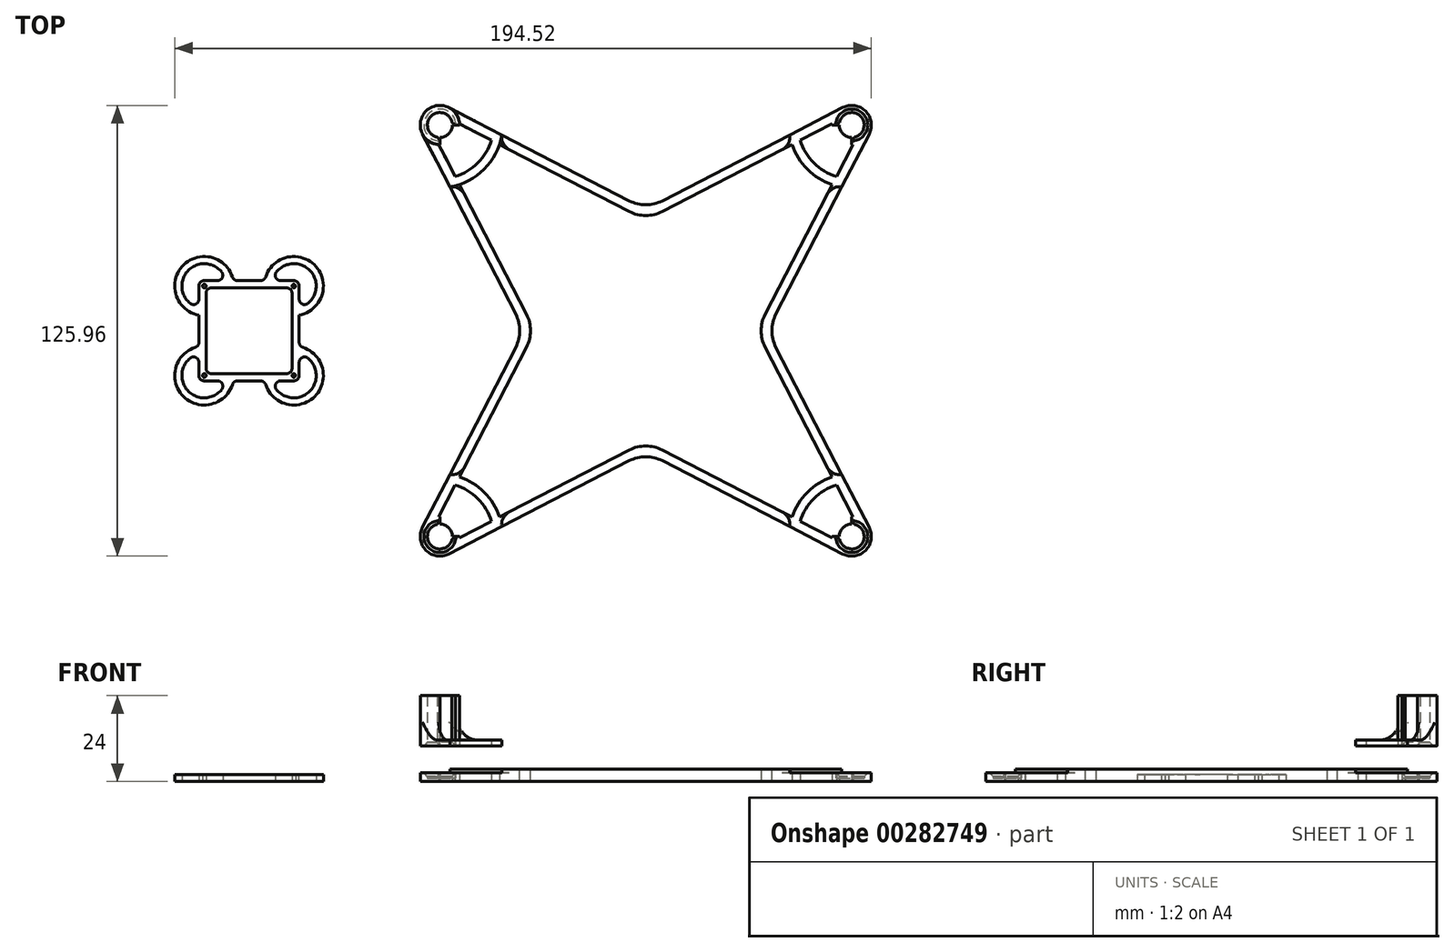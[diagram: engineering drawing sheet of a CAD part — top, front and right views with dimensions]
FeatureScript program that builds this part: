
annotation { "Feature Type Name" : "Feature", "Feature Type Description" : "" }
export const myFeature = defineFeature(function(context is Context, id is Id, definition is map)
    precondition{}
    {
        {
            var Q0;
            Q0=qCreatedBy(makeId("Top.planeOp"),FACE);
            var sketch = newSketch(context, id + "F0", { "sketchPlane" : qUnion([Q0])});
            skLineSegment(sketch, "E0.rect.bottom", {"start": v(57.5, 57.5) * mm, "end": v(-57.5, 57.5) * mm});
            skLineSegment(sketch, "E0.rect.top", {"start": v(57.5, -57.5) * mm, "end": v(-57.5, -57.5) * mm});
            skLineSegment(sketch, "E0.rect.left", {"start": v(57.5, 57.5) * mm, "end": v(57.5, -57.5) * mm});
            skLineSegment(sketch, "E0.rect.right", {"start": v(-57.5, 57.5) * mm, "end": v(-57.5, -57.5) * mm});
            skPoint(sketch, "E0.rect.middle", {"position": v(0, 0) * mm});
            skLineSegment(sketch, "E1", {"start": v(0, 33.94) * mm, "end": v(-33.94, 0) * mm});
            skLineSegment(sketch, "E2", {"start": v(-33.94, 0) * mm, "end": v(0, -33.94) * mm});
            skLineSegment(sketch, "E3", {"start": v(0, -33.94) * mm, "end": v(33.94, 0) * mm});
            skLineSegment(sketch, "E4", {"start": v(33.94, 0) * mm, "end": v(0, 33.94) * mm});
            skCircle(sketch, "E5", {"center": v(57.5, 57.5) * mm, "radius": 3.48 * mm});
            skCircle(sketch, "E6", {"center": v(57.5, 57.5) * mm, "radius": 5.47 * mm});
            skLineSegment(sketch, "E7", {"start": v(57.5, 60.98) * mm, "end": v(57.5, 62.98) * mm, "construction": true});
            skCircle(sketch, "E8", {"center": v(-57.5, 57.5) * mm, "radius": 3.48 * mm});
            skCircle(sketch, "E9", {"center": v(-57.5, 57.5) * mm, "radius": 5.47 * mm});
            skCircle(sketch, "E10", {"center": v(-57.5, -57.5) * mm, "radius": 3.48 * mm});
            skCircle(sketch, "E11", {"center": v(-57.5, -57.5) * mm, "radius": 5.47 * mm});
            skCircle(sketch, "E12", {"center": v(57.5, -57.5) * mm, "radius": 3.48 * mm});
            skCircle(sketch, "E13", {"center": v(57.5, -57.5) * mm, "radius": 5.47 * mm});
            skLineSegment(sketch, "E14", {"start": v(62.36, 54.99) * mm, "end": v(33.94, 0) * mm});
            skLineSegment(sketch, "E15", {"start": v(33.94, 0) * mm, "end": v(62.36, -54.99) * mm});
            skLineSegment(sketch, "E16", {"start": v(54.99, -62.36) * mm, "end": v(0, -33.94) * mm});
            skLineSegment(sketch, "E17", {"start": v(0, -33.94) * mm, "end": v(-54.99, -62.36) * mm});
            skLineSegment(sketch, "E18", {"start": v(-62.36, -54.99) * mm, "end": v(-33.94, 0) * mm});
            skLineSegment(sketch, "E19", {"start": v(-33.94, 0) * mm, "end": v(-62.36, 54.99) * mm});
            skLineSegment(sketch, "E20", {"start": v(-54.99, 62.36) * mm, "end": v(0, 33.94) * mm});
            skLineSegment(sketch, "E21", {"start": v(0, 33.94) * mm, "end": v(54.99, 62.36) * mm});
            skLineSegment(sketch, "E22.0", {"start": v(30.94, 0) * mm, "end": v(0, 30.94) * mm});
            skLineSegment(sketch, "E22.1", {"start": v(0, -30.94) * mm, "end": v(30.94, 0) * mm});
            skLineSegment(sketch, "E22.2", {"start": v(-30.94, 0) * mm, "end": v(0, -30.94) * mm});
            skLineSegment(sketch, "E22.3", {"start": v(0, 30.94) * mm, "end": v(-30.94, 0) * mm});
            skLineSegment(sketch, "E23", {"start": v(-30.94, 0) * mm, "end": v(-57.84, 52.04) * mm});
            skLineSegment(sketch, "E24", {"start": v(-30.94, 0) * mm, "end": v(-57.84, -52.04) * mm});
            skLineSegment(sketch, "E25", {"start": v(30.94, 0) * mm, "end": v(33.94, 0) * mm, "construction": true});
            skLineSegment(sketch, "E26", {"start": v(0, -30.94) * mm, "end": v(-52.04, -57.84) * mm});
            skLineSegment(sketch, "E27", {"start": v(0, -30.94) * mm, "end": v(52.04, -57.84) * mm});
            skLineSegment(sketch, "E28", {"start": v(57.84, -52.04) * mm, "end": v(30.94, 0) * mm});
            skLineSegment(sketch, "E29", {"start": v(30.94, 0) * mm, "end": v(57.84, 52.04) * mm});
            skLineSegment(sketch, "E30", {"start": v(52.04, 57.84) * mm, "end": v(0, 30.94) * mm});
            skLineSegment(sketch, "E31", {"start": v(0, 30.94) * mm, "end": v(-52.04, 57.84) * mm});
            skCircle(sketch, "E32", {"center": v(57.5, 57.5) * mm, "radius": 15 * mm});
            skCircle(sketch, "E33", {"center": v(57.5, 57.5) * mm, "radius": 17.5 * mm});
            skLineSegment(sketch, "E34", {"start": v(57.5, 72.5) * mm, "end": v(57.5, 75) * mm, "construction": true});
            skCircle(sketch, "E35", {"center": v(-57.5, 57.5) * mm, "radius": 15 * mm});
            skCircle(sketch, "E36", {"center": v(-57.5, 57.5) * mm, "radius": 17.5 * mm});
            skCircle(sketch, "E37", {"center": v(-57.5, -57.5) * mm, "radius": 15 * mm});
            skCircle(sketch, "E38", {"center": v(-57.5, -57.5) * mm, "radius": 17.5 * mm});
            skCircle(sketch, "E39", {"center": v(57.5, -57.5) * mm, "radius": 15 * mm});
            skCircle(sketch, "E40", {"center": v(57.5, -57.5) * mm, "radius": 17.5 * mm});
            skLineSegment(sketch, "E41.rect.bottom", {"start": v(-98.29, 12.5) * mm, "end": v(-123.29, 12.5) * mm, "construction": true});
            skLineSegment(sketch, "E41.rect.top", {"start": v(-98.29, -12.5) * mm, "end": v(-123.29, -12.5) * mm, "construction": true});
            skLineSegment(sketch, "E41.rect.left", {"start": v(-98.29, 12.5) * mm, "end": v(-98.29, -12.5) * mm, "construction": true});
            skLineSegment(sketch, "E41.rect.right", {"start": v(-123.29, 12.5) * mm, "end": v(-123.29, -12.5) * mm, "construction": true});
            skPoint(sketch, "E41.rect.middle", {"position": v(-110.79, 0) * mm});
            skCircle(sketch, "E42", {"center": v(-98.29, 12.5) * mm, "radius": 0.5 * mm});
            skCircle(sketch, "E43", {"center": v(-98.29, -12.5) * mm, "radius": 0.5 * mm});
            skCircle(sketch, "E44", {"center": v(-123.29, -12.5) * mm, "radius": 0.5 * mm});
            skCircle(sketch, "E45", {"center": v(-123.29, 12.5) * mm, "radius": 0.5 * mm});
            skCircle(sketch, "E46", {"center": v(-98.29, 12.5) * mm, "radius": 6.25 * mm});
            skCircle(sketch, "E47", {"center": v(-123.29, 12.5) * mm, "radius": 6.25 * mm});
            skCircle(sketch, "E48", {"center": v(-123.29, -12.5) * mm, "radius": 6.25 * mm});
            skCircle(sketch, "E49", {"center": v(-98.29, -12.5) * mm, "radius": 6.25 * mm});
            skCircle(sketch, "E50", {"center": v(-98.29, 12.5) * mm, "radius": 8.25 * mm});
            skLineSegment(sketch, "E51", {"start": v(-98.29, 18.75) * mm, "end": v(-98.29, 20.75) * mm, "construction": true});
            skCircle(sketch, "E52", {"center": v(-123.29, 12.5) * mm, "radius": 8.25 * mm});
            skCircle(sketch, "E53", {"center": v(-123.29, -12.5) * mm, "radius": 8.25 * mm});
            skCircle(sketch, "E54", {"center": v(-98.29, -12.5) * mm, "radius": 8.25 * mm});
            skLineSegment(sketch, "E55.rect.bottom", {"start": v(-96.79, 14) * mm, "end": v(-124.79, 14) * mm});
            skLineSegment(sketch, "E55.rect.top", {"start": v(-96.79, -14) * mm, "end": v(-124.79, -14) * mm});
            skLineSegment(sketch, "E55.rect.left", {"start": v(-96.79, 14) * mm, "end": v(-96.79, -14) * mm});
            skLineSegment(sketch, "E55.rect.right", {"start": v(-124.79, 14) * mm, "end": v(-124.79, -14) * mm});
            skLineSegment(sketch, "E56.rect.bottom", {"start": v(-98.79, 12) * mm, "end": v(-122.79, 12) * mm});
            skLineSegment(sketch, "E56.rect.top", {"start": v(-98.79, -12) * mm, "end": v(-122.79, -12) * mm});
            skLineSegment(sketch, "E56.rect.left", {"start": v(-98.79, 12) * mm, "end": v(-98.79, -12) * mm});
            skLineSegment(sketch, "E56.rect.right", {"start": v(-122.79, 12) * mm, "end": v(-122.79, -12) * mm});
            skLineSegment(sketch, "E57", {"start": v(-110.79, 12.5) * mm, "end": v(-110.79, 14) * mm, "construction": true});
            skLineSegment(sketch, "E58", {"start": v(-110.79, 12.5) * mm, "end": v(-110.79, 12) * mm, "construction": true});
            skCircle(sketch, "E59.cCircle", {"center": v(-110.79, 0) * mm, "radius": 17.68 * mm, "construction": true});
            skLineSegment(sketch, "E59.0", {"start": v(-110.79, 25) * mm, "end": v(-85.79, 0) * mm});
            skLineSegment(sketch, "E59.1", {"start": v(-85.79, 0) * mm, "end": v(-110.79, -25) * mm});
            skLineSegment(sketch, "E59.2", {"start": v(-110.79, -25) * mm, "end": v(-135.79, 0) * mm});
            skLineSegment(sketch, "E59.3", {"start": v(-135.79, 0) * mm, "end": v(-110.79, 25) * mm});
            skLineSegment(sketch, "E60", {"start": v(-124.79, 14) * mm, "end": v(-124.79, 20.61) * mm});
            skLineSegment(sketch, "E61", {"start": v(-122.79, 14) * mm, "end": v(-122.79, 20.73) * mm});
            skLineSegment(sketch, "E62", {"start": v(-98.79, 14) * mm, "end": v(-98.79, 20.73) * mm});
            skLineSegment(sketch, "E63", {"start": v(-96.79, 14) * mm, "end": v(-96.79, 20.61) * mm});
            skLineSegment(sketch, "E64", {"start": v(-124.79, -14) * mm, "end": v(-124.79, -20.61) * mm});
            skLineSegment(sketch, "E65", {"start": v(-122.79, -14) * mm, "end": v(-122.79, -20.73) * mm});
            skLineSegment(sketch, "E66", {"start": v(-98.79, -14) * mm, "end": v(-98.79, -20.73) * mm});
            skLineSegment(sketch, "E67", {"start": v(-96.79, -14) * mm, "end": v(-96.79, -20.61) * mm});
            skSolve(sketch);
        }
        {
            var Q0;
            {var subQ0=sQuery(id+"F0.wireOp",EDGE,"E9");var subQ7=sQuery(id+"F0.wireOp",EDGE,"E0.rect.bottom");var subQ8=makeQuery(id+"F0.imprint","INTERSECT",VERTEX,{"derivedFrom":[subQ7,subQ0]});Q0=makeQuery(id+"F0.imprint","IMPRINT",FACE,{"disambiguationData":[TD([[makeQuery(id+"F0.imprint","IMPRINT",EDGE,{"disambiguationData":[TD([[subQ8,-1.0]])],"derivedFrom":subQ7}),-1.0]])]});}
            var Q1;
            {var subQ1=sQuery(id+"F0.wireOp",EDGE,"E0.rect.right");var subQ5=sQuery(id+"F0.wireOp",EDGE,"E23");var subQ6=makeQuery(id+"F0.imprint","INTERSECT",VERTEX,{"derivedFrom":[subQ1,subQ5]});Q1=makeQuery(id+"F0.imprint","IMPRINT",FACE,{"disambiguationData":[TD([[makeQuery(id+"F0.imprint","IMPRINT",EDGE,{"disambiguationData":[TD([[subQ6,-1.0]])],"derivedFrom":subQ1}),-1.0]])]});}
            var Q2;
            {var subQ1=sQuery(id+"F0.wireOp",EDGE,"E23");var subQ5=sQuery(id+"F0.wireOp",EDGE,"E0.rect.right");var subQ6=makeQuery(id+"F0.imprint","INTERSECT",VERTEX,{"derivedFrom":[subQ5,subQ1]});Q2=makeQuery(id+"F0.imprint","IMPRINT",FACE,{"disambiguationData":[TD([[makeQuery(id+"F0.imprint","IMPRINT",EDGE,{"disambiguationData":[TD([[subQ6,-1.0]])],"derivedFrom":subQ5}),1.0]])]});}
            var Q3;
            {var subQ1=sQuery(id+"F0.wireOp",EDGE,"E0.rect.bottom");var subQ5=sQuery(id+"F0.wireOp",EDGE,"E20");var subQ6=makeQuery(id+"F0.imprint","INTERSECT",VERTEX,{"derivedFrom":[subQ1,subQ5]});Q3=makeQuery(id+"F0.imprint","IMPRINT",FACE,{"disambiguationData":[TD([[makeQuery(id+"F0.imprint","IMPRINT",EDGE,{"disambiguationData":[TD([[subQ6,-1.0]])],"derivedFrom":subQ1}),-1.0]])]});}
            var Q4;
            {var subQ3=sQuery(id+"F0.wireOp",EDGE,"E20");var subQ5=sQuery(id+"F0.wireOp",EDGE,"E0.rect.bottom");var subQ7=makeQuery(id+"F0.imprint","INTERSECT",VERTEX,{"derivedFrom":[subQ5,subQ3]});Q4=makeQuery(id+"F0.imprint","IMPRINT",FACE,{"disambiguationData":[TD([[makeQuery(id+"F0.imprint","IMPRINT",EDGE,{"disambiguationData":[TD([[subQ7,-1.0]])],"derivedFrom":subQ5}),1.0]])]});}
            var Q5;
            {var subQ0=sQuery(id+"F0.wireOp",EDGE,"E36");var subQ3=sQuery(id+"F0.wireOp",EDGE,"E19");var subQ4=makeQuery(id+"F0.imprint","INTERSECT",VERTEX,{"derivedFrom":[subQ3,subQ0]});Q5=makeQuery(id+"F0.imprint","IMPRINT",FACE,{"disambiguationData":[TD([[makeQuery(id+"F0.imprint","IMPRINT",EDGE,{"disambiguationData":[TD([[subQ4,-1.0]])],"derivedFrom":subQ3}),-1.0]])]});}
            var Q6;
            {var subQ3=sQuery(id+"F0.wireOp",EDGE,"E23");var subQ5=sQuery(id+"F0.wireOp",EDGE,"E36");var subQ7=makeQuery(id+"F0.imprint","INTERSECT",VERTEX,{"derivedFrom":[subQ3,subQ5]});Q6=makeQuery(id+"F0.imprint","IMPRINT",FACE,{"disambiguationData":[TD([[makeQuery(id+"F0.imprint","IMPRINT",EDGE,{"disambiguationData":[TD([[subQ7,-1.0]])],"derivedFrom":subQ3}),-1.0]])]});}
            var Q7;
            {var subQ3=sQuery(id+"F0.wireOp",EDGE,"E20");var subQ5=sQuery(id+"F0.wireOp",EDGE,"E35");var subQ7=makeQuery(id+"F0.imprint","INTERSECT",VERTEX,{"derivedFrom":[subQ3,subQ5]});Q7=makeQuery(id+"F0.imprint","IMPRINT",FACE,{"disambiguationData":[TD([[makeQuery(id+"F0.imprint","IMPRINT",EDGE,{"disambiguationData":[TD([[subQ7,-1.0]])],"derivedFrom":subQ3}),-1.0]])]});}
            extrude(context, id + "F1", {"entities" : qUnion([Q0, Q1, Q2, Q3, Q4, Q5, Q6, Q7]), "depth" : 1.6 * mm});
        }
        {
            var Q0;
            {var subQ0=sQuery(id+"F0.wireOp",EDGE,"E9");var subQ7=sQuery(id+"F0.wireOp",EDGE,"E0.rect.bottom");var subQ8=makeQuery(id+"F0.imprint","INTERSECT",VERTEX,{"derivedFrom":[subQ7,subQ0]});Q0=makeQuery(id+"F0.imprint","IMPRINT",FACE,{"disambiguationData":[TD([[makeQuery(id+"F0.imprint","IMPRINT",EDGE,{"disambiguationData":[TD([[subQ8,-1.0]])],"derivedFrom":subQ7}),-1.0]])]});}
            extrude(context, id + "F2", {"entities" : qUnion([Q0]), "operationType" : NewBodyOperationType.ADD, "depth" : 14 * mm});
        }
        {
            var Q0;
            {var subQ0=sQuery(id+"F0.wireOp",EDGE,"E9");Q0=makeQuery(id+"F2.boolean.opBoolean","INTERSECT",EDGE,{"disambiguationData":[OD(0.0)],"derivedFrom":[makeQuery(id+"F1.opExtrude","CAP_FACE",FACE,{"disambiguationData":[OSD([sQuery(id+"F0.wireOp",EDGE,"E0.rect.bottom"),sQuery(id+"F0.wireOp",EDGE,"E0.rect.right"),sQuery(id+"F0.wireOp",EDGE,"E8"),subQ0,sQuery(id+"F0.wireOp",EDGE,"E19"),sQuery(id+"F0.wireOp",EDGE,"E20"),sQuery(id+"F0.wireOp",EDGE,"E23"),sQuery(id+"F0.wireOp",EDGE,"E31"),sQuery(id+"F0.wireOp",EDGE,"E35"),sQuery(id+"F0.wireOp",EDGE,"E36")])],"isStart":false}),makeQuery(id+"F2.opExtrude","SWEPT_FACE",FACE,{"disambiguationData":[OSD([subQ0])]})]});}
            var Q1;
            {var subQ0=sQuery(id+"F0.wireOp",EDGE,"E9");Q1=makeQuery(id+"F2.boolean.opBoolean","INTERSECT",EDGE,{"disambiguationData":[OD(1.0)],"derivedFrom":[makeQuery(id+"F1.opExtrude","CAP_FACE",FACE,{"disambiguationData":[OSD([sQuery(id+"F0.wireOp",EDGE,"E0.rect.bottom"),sQuery(id+"F0.wireOp",EDGE,"E0.rect.right"),sQuery(id+"F0.wireOp",EDGE,"E8"),subQ0,sQuery(id+"F0.wireOp",EDGE,"E19"),sQuery(id+"F0.wireOp",EDGE,"E20"),sQuery(id+"F0.wireOp",EDGE,"E23"),sQuery(id+"F0.wireOp",EDGE,"E31"),sQuery(id+"F0.wireOp",EDGE,"E35"),sQuery(id+"F0.wireOp",EDGE,"E36")])],"isStart":false}),makeQuery(id+"F2.opExtrude","SWEPT_FACE",FACE,{"disambiguationData":[OSD([subQ0])]})]});}
            fillet(context, id + "F3", {"entities" : qUnion([Q0, Q1]), "radius" : 5 * mm, "tangentPropagation" : true, "allowEdgeOverflow" : false});
        }
        {
            var Q0;
            Q0=makeQuery(id+"F1.opExtrude","SWEPT_BODY",BODY,{"disambiguationData":[OSD([sQuery(id+"F0.wireOp",EDGE,"E0.rect.bottom"),sQuery(id+"F0.wireOp",EDGE,"E0.rect.right"),sQuery(id+"F0.wireOp",EDGE,"E8"),sQuery(id+"F0.wireOp",EDGE,"E9"),sQuery(id+"F0.wireOp",EDGE,"E19"),sQuery(id+"F0.wireOp",EDGE,"E20"),sQuery(id+"F0.wireOp",EDGE,"E23"),sQuery(id+"F0.wireOp",EDGE,"E31"),sQuery(id+"F0.wireOp",EDGE,"E35"),sQuery(id+"F0.wireOp",EDGE,"E36")])]});
            transform(context, id + "F4", {"entities" : qUnion([Q0]), "transformType" : TransformType.TRANSLATION_3D, "dx" : 0 * mm, "dy" : 0 * mm, "dz" : 10 * mm, "makeCopy" : false});
        }
        {
            var Q0;
            {var subQ1=sQuery(id+"F0.wireOp",EDGE,"E23");var subQ5=sQuery(id+"F0.wireOp",EDGE,"E0.rect.right");var subQ6=makeQuery(id+"F0.imprint","INTERSECT",VERTEX,{"derivedFrom":[subQ5,subQ1]});Q0=makeQuery(id+"F0.imprint","IMPRINT",FACE,{"disambiguationData":[TD([[makeQuery(id+"F0.imprint","IMPRINT",EDGE,{"disambiguationData":[TD([[subQ6,-1.0]])],"derivedFrom":subQ5}),1.0]])]});}
            var Q1;
            {var subQ1=sQuery(id+"F0.wireOp",EDGE,"E0.rect.right");var subQ5=sQuery(id+"F0.wireOp",EDGE,"E23");var subQ6=makeQuery(id+"F0.imprint","INTERSECT",VERTEX,{"derivedFrom":[subQ1,subQ5]});Q1=makeQuery(id+"F0.imprint","IMPRINT",FACE,{"disambiguationData":[TD([[makeQuery(id+"F0.imprint","IMPRINT",EDGE,{"disambiguationData":[TD([[subQ6,-1.0]])],"derivedFrom":subQ1}),-1.0]])]});}
            var Q2;
            {var subQ0=sQuery(id+"F0.wireOp",EDGE,"E9");var subQ7=sQuery(id+"F0.wireOp",EDGE,"E0.rect.bottom");var subQ8=makeQuery(id+"F0.imprint","INTERSECT",VERTEX,{"derivedFrom":[subQ7,subQ0]});Q2=makeQuery(id+"F0.imprint","IMPRINT",FACE,{"disambiguationData":[TD([[makeQuery(id+"F0.imprint","IMPRINT",EDGE,{"disambiguationData":[TD([[subQ8,-1.0]])],"derivedFrom":subQ7}),-1.0]])]});}
            var Q3;
            {var subQ1=sQuery(id+"F0.wireOp",EDGE,"E0.rect.bottom");var subQ5=sQuery(id+"F0.wireOp",EDGE,"E20");var subQ6=makeQuery(id+"F0.imprint","INTERSECT",VERTEX,{"derivedFrom":[subQ1,subQ5]});Q3=makeQuery(id+"F0.imprint","IMPRINT",FACE,{"disambiguationData":[TD([[makeQuery(id+"F0.imprint","IMPRINT",EDGE,{"disambiguationData":[TD([[subQ6,-1.0]])],"derivedFrom":subQ1}),-1.0]])]});}
            var Q4;
            {var subQ3=sQuery(id+"F0.wireOp",EDGE,"E20");var subQ5=sQuery(id+"F0.wireOp",EDGE,"E0.rect.bottom");var subQ7=makeQuery(id+"F0.imprint","INTERSECT",VERTEX,{"derivedFrom":[subQ5,subQ3]});Q4=makeQuery(id+"F0.imprint","IMPRINT",FACE,{"disambiguationData":[TD([[makeQuery(id+"F0.imprint","IMPRINT",EDGE,{"disambiguationData":[TD([[subQ7,-1.0]])],"derivedFrom":subQ5}),1.0]])]});}
            var Q5;
            {var subQ0=sQuery(id+"F0.wireOp",EDGE,"E36");var subQ3=sQuery(id+"F0.wireOp",EDGE,"E19");var subQ4=makeQuery(id+"F0.imprint","INTERSECT",VERTEX,{"derivedFrom":[subQ3,subQ0]});Q5=makeQuery(id+"F0.imprint","IMPRINT",FACE,{"disambiguationData":[TD([[makeQuery(id+"F0.imprint","IMPRINT",EDGE,{"disambiguationData":[TD([[subQ4,-1.0]])],"derivedFrom":subQ3}),-1.0]])]});}
            var Q6;
            {var subQ3=sQuery(id+"F0.wireOp",EDGE,"E20");var subQ5=sQuery(id+"F0.wireOp",EDGE,"E35");var subQ7=makeQuery(id+"F0.imprint","INTERSECT",VERTEX,{"derivedFrom":[subQ3,subQ5]});Q6=makeQuery(id+"F0.imprint","IMPRINT",FACE,{"disambiguationData":[TD([[makeQuery(id+"F0.imprint","IMPRINT",EDGE,{"disambiguationData":[TD([[subQ7,-1.0]])],"derivedFrom":subQ3}),-1.0]])]});}
            var Q7;
            {var subQ0=sQuery(id+"F0.wireOp",EDGE,"E33");var subQ3=sQuery(id+"F0.wireOp",EDGE,"E21");var subQ4=makeQuery(id+"F0.imprint","INTERSECT",VERTEX,{"derivedFrom":[subQ3,subQ0]});Q7=makeQuery(id+"F0.imprint","IMPRINT",FACE,{"disambiguationData":[TD([[makeQuery(id+"F0.imprint","IMPRINT",EDGE,{"disambiguationData":[TD([[subQ4,-1.0]])],"derivedFrom":subQ3}),-1.0]])]});}
            var Q8;
            {var subQ1=sQuery(id+"F0.wireOp",EDGE,"E30");var subQ5=sQuery(id+"F0.wireOp",EDGE,"E0.rect.bottom");var subQ6=makeQuery(id+"F0.imprint","INTERSECT",VERTEX,{"derivedFrom":[subQ5,subQ1]});Q8=makeQuery(id+"F0.imprint","IMPRINT",FACE,{"disambiguationData":[TD([[makeQuery(id+"F0.imprint","IMPRINT",EDGE,{"disambiguationData":[TD([[subQ6,-1.0]])],"derivedFrom":subQ5}),1.0]])]});}
            var Q9;
            {var subQ0=sQuery(id+"F0.wireOp",EDGE,"E30");var subQ1=sQuery(id+"F0.wireOp",EDGE,"E0.rect.bottom");var subQ2=makeQuery(id+"F0.imprint","INTERSECT",VERTEX,{"derivedFrom":[subQ1,subQ0]});Q9=makeQuery(id+"F0.imprint","IMPRINT",FACE,{"disambiguationData":[TD([[makeQuery(id+"F0.imprint","IMPRINT",EDGE,{"disambiguationData":[TD([[subQ2,-1.0]])],"derivedFrom":subQ1}),-1.0]])]});}
            var Q10;
            {var subQ7=sQuery(id+"F0.wireOp",EDGE,"E5");var subQ9=sQuery(id+"F0.wireOp",EDGE,"E0.rect.bottom");var subQ10=makeQuery(id+"F0.imprint","INTERSECT",VERTEX,{"derivedFrom":[subQ9,subQ7]});Q10=makeQuery(id+"F0.imprint","IMPRINT",FACE,{"disambiguationData":[TD([[makeQuery(id+"F0.imprint","IMPRINT",EDGE,{"disambiguationData":[TD([[subQ10,-1.0]])],"derivedFrom":subQ9}),-1.0]])]});}
            var Q11;
            {var subQ0=sQuery(id+"F0.wireOp",EDGE,"E29");var subQ1=sQuery(id+"F0.wireOp",EDGE,"E0.rect.left");var subQ2=makeQuery(id+"F0.imprint","INTERSECT",VERTEX,{"derivedFrom":[subQ1,subQ0]});Q11=makeQuery(id+"F0.imprint","IMPRINT",FACE,{"disambiguationData":[TD([[makeQuery(id+"F0.imprint","IMPRINT",EDGE,{"disambiguationData":[TD([[subQ2,-1.0]])],"derivedFrom":subQ1}),1.0]])]});}
            var Q12;
            {var subQ1=sQuery(id+"F0.wireOp",EDGE,"E29");var subQ5=sQuery(id+"F0.wireOp",EDGE,"E0.rect.left");var subQ6=makeQuery(id+"F0.imprint","INTERSECT",VERTEX,{"derivedFrom":[subQ5,subQ1]});Q12=makeQuery(id+"F0.imprint","IMPRINT",FACE,{"disambiguationData":[TD([[makeQuery(id+"F0.imprint","IMPRINT",EDGE,{"disambiguationData":[TD([[subQ6,-1.0]])],"derivedFrom":subQ5}),-1.0]])]});}
            var Q13;
            {var subQ3=sQuery(id+"F0.wireOp",EDGE,"E14");var subQ5=sQuery(id+"F0.wireOp",EDGE,"E32");var subQ7=makeQuery(id+"F0.imprint","INTERSECT",VERTEX,{"derivedFrom":[subQ3,subQ5]});Q13=makeQuery(id+"F0.imprint","IMPRINT",FACE,{"disambiguationData":[TD([[makeQuery(id+"F0.imprint","IMPRINT",EDGE,{"disambiguationData":[TD([[subQ7,-1.0]])],"derivedFrom":subQ3}),-1.0]])]});}
            var Q14;
            {var subQ0=sQuery(id+"F0.wireOp",EDGE,"E40");var subQ3=sQuery(id+"F0.wireOp",EDGE,"E15");var subQ4=makeQuery(id+"F0.imprint","INTERSECT",VERTEX,{"derivedFrom":[subQ3,subQ0]});Q14=makeQuery(id+"F0.imprint","IMPRINT",FACE,{"disambiguationData":[TD([[makeQuery(id+"F0.imprint","IMPRINT",EDGE,{"disambiguationData":[TD([[subQ4,-1.0]])],"derivedFrom":subQ3}),-1.0]])]});}
            var Q15;
            {var subQ3=sQuery(id+"F0.wireOp",EDGE,"E18");var subQ5=sQuery(id+"F0.wireOp",EDGE,"E37");var subQ7=makeQuery(id+"F0.imprint","INTERSECT",VERTEX,{"derivedFrom":[subQ3,subQ5]});Q15=makeQuery(id+"F0.imprint","IMPRINT",FACE,{"disambiguationData":[TD([[makeQuery(id+"F0.imprint","IMPRINT",EDGE,{"disambiguationData":[TD([[subQ7,-1.0]])],"derivedFrom":subQ3}),-1.0]])]});}
            var Q16;
            {var subQ3=sQuery(id+"F0.wireOp",EDGE,"E18");var subQ5=sQuery(id+"F0.wireOp",EDGE,"E0.rect.right");var subQ7=makeQuery(id+"F0.imprint","INTERSECT",VERTEX,{"derivedFrom":[subQ5,subQ3]});Q16=makeQuery(id+"F0.imprint","IMPRINT",FACE,{"disambiguationData":[TD([[makeQuery(id+"F0.imprint","IMPRINT",EDGE,{"disambiguationData":[TD([[subQ7,-1.0]])],"derivedFrom":subQ5}),1.0]])]});}
            var Q17;
            {var subQ1=sQuery(id+"F0.wireOp",EDGE,"E0.rect.right");var subQ5=sQuery(id+"F0.wireOp",EDGE,"E18");var subQ6=makeQuery(id+"F0.imprint","INTERSECT",VERTEX,{"derivedFrom":[subQ1,subQ5]});Q17=makeQuery(id+"F0.imprint","IMPRINT",FACE,{"disambiguationData":[TD([[makeQuery(id+"F0.imprint","IMPRINT",EDGE,{"disambiguationData":[TD([[subQ6,-1.0]])],"derivedFrom":subQ1}),-1.0]])]});}
            var Q18;
            {var subQ0=sQuery(id+"F0.wireOp",EDGE,"E11");var subQ1=sQuery(id+"F0.wireOp",EDGE,"E0.rect.top");var subQ2=makeQuery(id+"F0.imprint","INTERSECT",VERTEX,{"derivedFrom":[subQ1,subQ0]});Q18=makeQuery(id+"F0.imprint","IMPRINT",FACE,{"disambiguationData":[TD([[makeQuery(id+"F0.imprint","IMPRINT",EDGE,{"disambiguationData":[TD([[subQ2,-1.0]])],"derivedFrom":subQ1}),1.0]])]});}
            var Q19;
            {var subQ1=sQuery(id+"F0.wireOp",EDGE,"E0.rect.top");var subQ5=sQuery(id+"F0.wireOp",EDGE,"E17");var subQ6=makeQuery(id+"F0.imprint","INTERSECT",VERTEX,{"derivedFrom":[subQ1,subQ5]});Q19=makeQuery(id+"F0.imprint","IMPRINT",FACE,{"disambiguationData":[TD([[makeQuery(id+"F0.imprint","IMPRINT",EDGE,{"disambiguationData":[TD([[subQ6,-1.0]])],"derivedFrom":subQ1}),1.0]])]});}
            var Q20;
            {var subQ3=sQuery(id+"F0.wireOp",EDGE,"E17");var subQ5=sQuery(id+"F0.wireOp",EDGE,"E0.rect.top");var subQ7=makeQuery(id+"F0.imprint","INTERSECT",VERTEX,{"derivedFrom":[subQ5,subQ3]});Q20=makeQuery(id+"F0.imprint","IMPRINT",FACE,{"disambiguationData":[TD([[makeQuery(id+"F0.imprint","IMPRINT",EDGE,{"disambiguationData":[TD([[subQ7,-1.0]])],"derivedFrom":subQ5}),-1.0]])]});}
            var Q21;
            {var subQ0=sQuery(id+"F0.wireOp",EDGE,"E38");var subQ3=sQuery(id+"F0.wireOp",EDGE,"E17");var subQ4=makeQuery(id+"F0.imprint","INTERSECT",VERTEX,{"derivedFrom":[subQ3,subQ0]});Q21=makeQuery(id+"F0.imprint","IMPRINT",FACE,{"disambiguationData":[TD([[makeQuery(id+"F0.imprint","IMPRINT",EDGE,{"disambiguationData":[TD([[subQ4,-1.0]])],"derivedFrom":subQ3}),-1.0]])]});}
            var Q22;
            {var subQ3=sQuery(id+"F0.wireOp",EDGE,"E16");var subQ5=sQuery(id+"F0.wireOp",EDGE,"E39");var subQ7=makeQuery(id+"F0.imprint","INTERSECT",VERTEX,{"derivedFrom":[subQ3,subQ5]});Q22=makeQuery(id+"F0.imprint","IMPRINT",FACE,{"disambiguationData":[TD([[makeQuery(id+"F0.imprint","IMPRINT",EDGE,{"disambiguationData":[TD([[subQ7,-1.0]])],"derivedFrom":subQ3}),-1.0]])]});}
            var Q23;
            {var subQ3=sQuery(id+"F0.wireOp",EDGE,"E0.rect.top");var subQ9=sQuery(id+"F0.wireOp",EDGE,"E12");var subQ11=makeQuery(id+"F0.imprint","INTERSECT",VERTEX,{"derivedFrom":[subQ3,subQ9]});Q23=makeQuery(id+"F0.imprint","IMPRINT",FACE,{"disambiguationData":[TD([[makeQuery(id+"F0.imprint","IMPRINT",EDGE,{"disambiguationData":[TD([[subQ11,-1.0]])],"derivedFrom":subQ3}),1.0]])]});}
            var Q24;
            {var subQ1=sQuery(id+"F0.wireOp",EDGE,"E0.rect.top");var subQ5=sQuery(id+"F0.wireOp",EDGE,"E27");var subQ6=makeQuery(id+"F0.imprint","INTERSECT",VERTEX,{"derivedFrom":[subQ1,subQ5]});Q24=makeQuery(id+"F0.imprint","IMPRINT",FACE,{"disambiguationData":[TD([[makeQuery(id+"F0.imprint","IMPRINT",EDGE,{"disambiguationData":[TD([[subQ6,-1.0]])],"derivedFrom":subQ1}),1.0]])]});}
            var Q25;
            {var subQ1=sQuery(id+"F0.wireOp",EDGE,"E27");var subQ5=sQuery(id+"F0.wireOp",EDGE,"E0.rect.top");var subQ6=makeQuery(id+"F0.imprint","INTERSECT",VERTEX,{"derivedFrom":[subQ5,subQ1]});Q25=makeQuery(id+"F0.imprint","IMPRINT",FACE,{"disambiguationData":[TD([[makeQuery(id+"F0.imprint","IMPRINT",EDGE,{"disambiguationData":[TD([[subQ6,-1.0]])],"derivedFrom":subQ5}),-1.0]])]});}
            var Q26;
            {var subQ1=sQuery(id+"F0.wireOp",EDGE,"E0.rect.left");var subQ5=sQuery(id+"F0.wireOp",EDGE,"E15");var subQ6=makeQuery(id+"F0.imprint","INTERSECT",VERTEX,{"derivedFrom":[subQ1,subQ5]});Q26=makeQuery(id+"F0.imprint","IMPRINT",FACE,{"disambiguationData":[TD([[makeQuery(id+"F0.imprint","IMPRINT",EDGE,{"disambiguationData":[TD([[subQ6,-1.0]])],"derivedFrom":subQ1}),1.0]])]});}
            var Q27;
            {var subQ3=sQuery(id+"F0.wireOp",EDGE,"E15");var subQ5=sQuery(id+"F0.wireOp",EDGE,"E0.rect.left");var subQ7=makeQuery(id+"F0.imprint","INTERSECT",VERTEX,{"derivedFrom":[subQ5,subQ3]});Q27=makeQuery(id+"F0.imprint","IMPRINT",FACE,{"disambiguationData":[TD([[makeQuery(id+"F0.imprint","IMPRINT",EDGE,{"disambiguationData":[TD([[subQ7,-1.0]])],"derivedFrom":subQ5}),-1.0]])]});}
            var Q28;
            {var subQ3=sQuery(id+"F0.wireOp",EDGE,"E23");var subQ5=sQuery(id+"F0.wireOp",EDGE,"E36");var subQ7=makeQuery(id+"F0.imprint","INTERSECT",VERTEX,{"derivedFrom":[subQ3,subQ5]});Q28=makeQuery(id+"F0.imprint","IMPRINT",FACE,{"disambiguationData":[TD([[makeQuery(id+"F0.imprint","IMPRINT",EDGE,{"disambiguationData":[TD([[subQ7,-1.0]])],"derivedFrom":subQ3}),-1.0]])]});}
            var Q29;
            {var subQ0=sQuery(id+"F0.wireOp",EDGE,"E33");var subQ3=sQuery(id+"F0.wireOp",EDGE,"E29");var subQ4=makeQuery(id+"F0.imprint","INTERSECT",VERTEX,{"derivedFrom":[subQ3,subQ0]});Q29=makeQuery(id+"F0.imprint","IMPRINT",FACE,{"disambiguationData":[TD([[makeQuery(id+"F0.imprint","IMPRINT",EDGE,{"disambiguationData":[TD([[subQ4,-1.0]])],"derivedFrom":subQ3}),1.0]])]});}
            var Q30;
            {var subQ0=sQuery(id+"F0.wireOp",EDGE,"E40");var subQ3=sQuery(id+"F0.wireOp",EDGE,"E27");var subQ4=makeQuery(id+"F0.imprint","INTERSECT",VERTEX,{"derivedFrom":[subQ3,subQ0]});Q30=makeQuery(id+"F0.imprint","IMPRINT",FACE,{"disambiguationData":[TD([[makeQuery(id+"F0.imprint","IMPRINT",EDGE,{"disambiguationData":[TD([[subQ4,-1.0]])],"derivedFrom":subQ3}),1.0]])]});}
            var Q31;
            {var subQ0=sQuery(id+"F0.wireOp",EDGE,"E38");var subQ3=sQuery(id+"F0.wireOp",EDGE,"E24");var subQ4=makeQuery(id+"F0.imprint","INTERSECT",VERTEX,{"derivedFrom":[subQ3,subQ0]});Q31=makeQuery(id+"F0.imprint","IMPRINT",FACE,{"disambiguationData":[TD([[makeQuery(id+"F0.imprint","IMPRINT",EDGE,{"disambiguationData":[TD([[subQ4,-1.0]])],"derivedFrom":subQ3}),1.0]])]});}
            extrude(context, id + "F5", {"entities" : qUnion([Q0, Q1, Q2, Q3, Q4, Q5, Q6, Q7, Q8, Q9, Q10, Q11, Q12, Q13, Q14, Q15, Q16, Q17, Q18, Q19, Q20, Q21, Q22, Q23, Q24, Q25, Q26, Q27, Q28, Q29, Q30, Q31]), "depth" : 2.5 * mm});
        }
        {
            var Q0;
            {var subQ1=sQuery(id+"F0.wireOp",EDGE,"E0.rect.right");var subQ3=sQuery(id+"F0.wireOp",EDGE,"E0.rect.bottom");var subQ5=makeQuery(id+"F0.imprint","INTERSECT",VERTEX,{"derivedFrom":[subQ3,subQ1]});Q0=makeQuery(id+"F0.imprint","IMPRINT",FACE,{"disambiguationData":[TD([[makeQuery(id+"F0.imprint","IMPRINT",EDGE,{"disambiguationData":[TD([[subQ5,1.0]])],"derivedFrom":subQ3}),-1.0]])]});}
            var Q1;
            {var subQ1=sQuery(id+"F0.wireOp",EDGE,"E0.rect.right");var subQ3=sQuery(id+"F0.wireOp",EDGE,"E0.rect.bottom");var subQ5=makeQuery(id+"F0.imprint","INTERSECT",VERTEX,{"derivedFrom":[subQ3,subQ1]});Q1=makeQuery(id+"F0.imprint","IMPRINT",FACE,{"disambiguationData":[TD([[makeQuery(id+"F0.imprint","IMPRINT",EDGE,{"disambiguationData":[TD([[subQ5,1.0]])],"derivedFrom":subQ3}),1.0]])]});}
            var Q2;
            {var subQ1=sQuery(id+"F0.wireOp",EDGE,"E0.rect.right");var subQ3=sQuery(id+"F0.wireOp",EDGE,"E0.rect.top");var subQ5=makeQuery(id+"F0.imprint","INTERSECT",VERTEX,{"derivedFrom":[subQ3,subQ1]});Q2=makeQuery(id+"F0.imprint","IMPRINT",FACE,{"disambiguationData":[TD([[makeQuery(id+"F0.imprint","IMPRINT",EDGE,{"disambiguationData":[TD([[subQ5,1.0]])],"derivedFrom":subQ3}),1.0]])]});}
            var Q3;
            {var subQ1=sQuery(id+"F0.wireOp",EDGE,"E0.rect.right");var subQ3=sQuery(id+"F0.wireOp",EDGE,"E0.rect.top");var subQ5=makeQuery(id+"F0.imprint","INTERSECT",VERTEX,{"derivedFrom":[subQ3,subQ1]});Q3=makeQuery(id+"F0.imprint","IMPRINT",FACE,{"disambiguationData":[TD([[makeQuery(id+"F0.imprint","IMPRINT",EDGE,{"disambiguationData":[TD([[subQ5,1.0]])],"derivedFrom":subQ3}),-1.0]])]});}
            var Q4;
            {var subQ1=sQuery(id+"F0.wireOp",EDGE,"E0.rect.left");var subQ3=sQuery(id+"F0.wireOp",EDGE,"E0.rect.top");var subQ5=makeQuery(id+"F0.imprint","INTERSECT",VERTEX,{"derivedFrom":[subQ3,subQ1]});Q4=makeQuery(id+"F0.imprint","IMPRINT",FACE,{"disambiguationData":[TD([[makeQuery(id+"F0.imprint","IMPRINT",EDGE,{"disambiguationData":[TD([[subQ5,-1.0]])],"derivedFrom":subQ3}),1.0]])]});}
            var Q5;
            {var subQ1=sQuery(id+"F0.wireOp",EDGE,"E0.rect.left");var subQ3=sQuery(id+"F0.wireOp",EDGE,"E0.rect.top");var subQ5=makeQuery(id+"F0.imprint","INTERSECT",VERTEX,{"derivedFrom":[subQ3,subQ1]});Q5=makeQuery(id+"F0.imprint","IMPRINT",FACE,{"disambiguationData":[TD([[makeQuery(id+"F0.imprint","IMPRINT",EDGE,{"disambiguationData":[TD([[subQ5,-1.0]])],"derivedFrom":subQ3}),-1.0]])]});}
            var Q6;
            {var subQ1=sQuery(id+"F0.wireOp",EDGE,"E0.rect.left");var subQ3=sQuery(id+"F0.wireOp",EDGE,"E0.rect.bottom");var subQ5=makeQuery(id+"F0.imprint","INTERSECT",VERTEX,{"derivedFrom":[subQ3,subQ1]});Q6=makeQuery(id+"F0.imprint","IMPRINT",FACE,{"disambiguationData":[TD([[makeQuery(id+"F0.imprint","IMPRINT",EDGE,{"disambiguationData":[TD([[subQ5,-1.0]])],"derivedFrom":subQ3}),-1.0]])]});}
            var Q7;
            {var subQ1=sQuery(id+"F0.wireOp",EDGE,"E0.rect.left");var subQ3=sQuery(id+"F0.wireOp",EDGE,"E0.rect.bottom");var subQ5=makeQuery(id+"F0.imprint","INTERSECT",VERTEX,{"derivedFrom":[subQ3,subQ1]});Q7=makeQuery(id+"F0.imprint","IMPRINT",FACE,{"disambiguationData":[TD([[makeQuery(id+"F0.imprint","IMPRINT",EDGE,{"disambiguationData":[TD([[subQ5,-1.0]])],"derivedFrom":subQ3}),1.0]])]});}
            extrude(context, id + "F6", {"entities" : qUnion([Q0, Q1, Q2, Q3, Q4, Q5, Q6, Q7]), "operationType" : NewBodyOperationType.ADD, "depth" : 1 * mm});
        }
        {
            var Q0;
            {var subQ0=sQuery(id+"F0.wireOp",EDGE,"E0.rect.right");var subQ1=sQuery(id+"F0.wireOp",EDGE,"E8");Q0=makeQuery(id+"F2.boolean.opBoolean","MERGE",EDGE,{"derivedFrom":[makeQuery(id+"F1.opExtrude","SWEPT_EDGE",EDGE,{"disambiguationData":[OSD([subQ0,subQ1])]}),makeQuery(id+"F2.opExtrude","SWEPT_EDGE",EDGE,{"disambiguationData":[OSD([subQ0,subQ1])]})]});}
            var Q1;
            {var subQ0=sQuery(id+"F0.wireOp",EDGE,"E0.rect.bottom");var subQ1=sQuery(id+"F0.wireOp",EDGE,"E8");Q1=makeQuery(id+"F2.boolean.opBoolean","MERGE",EDGE,{"derivedFrom":[makeQuery(id+"F1.opExtrude","SWEPT_EDGE",EDGE,{"disambiguationData":[OSD([subQ0,subQ1])]}),makeQuery(id+"F2.opExtrude","SWEPT_EDGE",EDGE,{"disambiguationData":[OSD([subQ0,subQ1])]})]});}
            var Q2;
            {var subQ0=sQuery(id+"F0.wireOp",EDGE,"E8");var subQ1=sQuery(id+"F0.wireOp",EDGE,"E0.rect.right");Q2=makeQuery(id+"F6.boolean.opBoolean","SPLIT",EDGE,{"disambiguationData":[topologyDisambiguationEdgeConnected([makeQuery(id+"F5.opExtrude","SWEPT_FACE",FACE,{"disambiguationData":[OSD([subQ0])]})])],"derivedFrom":makeQuery(id+"F5.opExtrude","SWEPT_EDGE",EDGE,{"disambiguationData":[OSD([subQ1,subQ0])]})});}
            var Q3;
            {var subQ0=sQuery(id+"F0.wireOp",EDGE,"E0.rect.bottom");var subQ1=sQuery(id+"F0.wireOp",EDGE,"E8");Q3=makeQuery(id+"F6.boolean.opBoolean","SPLIT",EDGE,{"disambiguationData":[topologyDisambiguationEdgeConnected([makeQuery(id+"F5.opExtrude","SWEPT_FACE",FACE,{"disambiguationData":[OSD([subQ1])]})])],"derivedFrom":makeQuery(id+"F5.opExtrude","SWEPT_EDGE",EDGE,{"disambiguationData":[OSD([subQ0,subQ1])]})});}
            var Q4;
            Q4=makeQuery(id+"F1.opExtrude","CAP_EDGE",EDGE,{"disambiguationData":[OSD([sQuery(id+"F0.wireOp",EDGE,"E8")])],"isStart":true});
            var Q5;
            Q5=makeQuery(id+"F5.opExtrude","CAP_EDGE",EDGE,{"disambiguationData":[OSD([sQuery(id+"F0.wireOp",EDGE,"E8")])],"isStart":false});
            var Q6;
            {var subQ0=sQuery(id+"F0.wireOp",EDGE,"E0.rect.right");var subQ1=sQuery(id+"F0.wireOp",EDGE,"E10");Q6=makeQuery(id+"F6.boolean.opBoolean","SPLIT",EDGE,{"disambiguationData":[topologyDisambiguationEdgeConnected([makeQuery(id+"F5.opExtrude","SWEPT_FACE",FACE,{"disambiguationData":[OSD([subQ1])]})])],"derivedFrom":makeQuery(id+"F5.opExtrude","SWEPT_EDGE",EDGE,{"disambiguationData":[OSD([subQ0,subQ1])]})});}
            var Q7;
            {var subQ0=sQuery(id+"F0.wireOp",EDGE,"E0.rect.top");var subQ1=sQuery(id+"F0.wireOp",EDGE,"E10");Q7=makeQuery(id+"F6.boolean.opBoolean","SPLIT",EDGE,{"disambiguationData":[topologyDisambiguationEdgeConnected([makeQuery(id+"F5.opExtrude","SWEPT_FACE",FACE,{"disambiguationData":[OSD([subQ1])]})])],"derivedFrom":makeQuery(id+"F5.opExtrude","SWEPT_EDGE",EDGE,{"disambiguationData":[OSD([subQ0,subQ1])]})});}
            var Q8;
            Q8=makeQuery(id+"F5.opExtrude","CAP_EDGE",EDGE,{"disambiguationData":[OSD([sQuery(id+"F0.wireOp",EDGE,"E10")])],"isStart":false});
            var Q9;
            {var subQ0=sQuery(id+"F0.wireOp",EDGE,"E12");var subQ1=sQuery(id+"F0.wireOp",EDGE,"E0.rect.top");Q9=makeQuery(id+"F6.boolean.opBoolean","SPLIT",EDGE,{"disambiguationData":[topologyDisambiguationEdgeConnected([makeQuery(id+"F5.opExtrude","SWEPT_FACE",FACE,{"disambiguationData":[OSD([subQ0])]})])],"derivedFrom":makeQuery(id+"F5.opExtrude","SWEPT_EDGE",EDGE,{"disambiguationData":[OSD([subQ1,subQ0])]})});}
            var Q10;
            {var subQ0=sQuery(id+"F0.wireOp",EDGE,"E0.rect.left");var subQ1=sQuery(id+"F0.wireOp",EDGE,"E12");Q10=makeQuery(id+"F6.boolean.opBoolean","SPLIT",EDGE,{"disambiguationData":[topologyDisambiguationEdgeConnected([makeQuery(id+"F5.opExtrude","SWEPT_FACE",FACE,{"disambiguationData":[OSD([subQ1])]})])],"derivedFrom":makeQuery(id+"F5.opExtrude","SWEPT_EDGE",EDGE,{"disambiguationData":[OSD([subQ0,subQ1])]})});}
            var Q11;
            Q11=makeQuery(id+"F5.opExtrude","CAP_EDGE",EDGE,{"disambiguationData":[OSD([sQuery(id+"F0.wireOp",EDGE,"E12")])],"isStart":false});
            var Q12;
            {var subQ0=sQuery(id+"F0.wireOp",EDGE,"E5");var subQ1=sQuery(id+"F0.wireOp",EDGE,"E0.rect.bottom");Q12=makeQuery(id+"F6.boolean.opBoolean","SPLIT",EDGE,{"disambiguationData":[topologyDisambiguationEdgeConnected([makeQuery(id+"F5.opExtrude","SWEPT_FACE",FACE,{"disambiguationData":[OSD([subQ0])]})])],"derivedFrom":makeQuery(id+"F5.opExtrude","SWEPT_EDGE",EDGE,{"disambiguationData":[OSD([subQ1,subQ0])]})});}
            var Q13;
            Q13=makeQuery(id+"F5.opExtrude","CAP_EDGE",EDGE,{"disambiguationData":[OSD([sQuery(id+"F0.wireOp",EDGE,"E5")])],"isStart":false});
            var Q14;
            {var subQ0=sQuery(id+"F0.wireOp",EDGE,"E5");var subQ1=sQuery(id+"F0.wireOp",EDGE,"E0.rect.left");Q14=makeQuery(id+"F6.boolean.opBoolean","SPLIT",EDGE,{"disambiguationData":[topologyDisambiguationEdgeConnected([makeQuery(id+"F5.opExtrude","SWEPT_FACE",FACE,{"disambiguationData":[OSD([subQ0])]})])],"derivedFrom":makeQuery(id+"F5.opExtrude","SWEPT_EDGE",EDGE,{"disambiguationData":[OSD([subQ1,subQ0])]})});}
            chamfer(context, id + "F7", {"entities" : qUnion([Q0, Q1, Q2, Q3, Q4, Q5, Q6, Q7, Q8, Q9, Q10, Q11, Q12, Q13, Q14]), "width" : 1 * mm, "tangentPropagation" : true});
        }
        {
            var Q0;
            {var subQ1=sQuery(id+"F0.wireOp",EDGE,"E23");var subQ5=sQuery(id+"F0.wireOp",EDGE,"E1");var subQ6=makeQuery(id+"F0.imprint","INTERSECT",VERTEX,{"derivedFrom":[subQ5,subQ1]});Q0=makeQuery(id+"F0.imprint","IMPRINT",FACE,{"disambiguationData":[TD([[makeQuery(id+"F0.imprint","IMPRINT",EDGE,{"disambiguationData":[TD([[subQ6,-1.0]])],"derivedFrom":subQ1}),1.0]])]});}
            var Q1;
            {var subQ1=sQuery(id+"F0.wireOp",EDGE,"E31");var subQ5=sQuery(id+"F0.wireOp",EDGE,"E1");var subQ6=makeQuery(id+"F0.imprint","INTERSECT",VERTEX,{"derivedFrom":[subQ5,subQ1]});Q1=makeQuery(id+"F0.imprint","IMPRINT",FACE,{"disambiguationData":[TD([[makeQuery(id+"F0.imprint","IMPRINT",EDGE,{"disambiguationData":[TD([[subQ6,-1.0]])],"derivedFrom":subQ1}),-1.0]])]});}
            var Q2;
            {var subQ0=sQuery(id+"F0.wireOp",EDGE,"E31");var subQ1=sQuery(id+"F0.wireOp",EDGE,"E1");var subQ2=makeQuery(id+"F0.imprint","INTERSECT",VERTEX,{"derivedFrom":[subQ1,subQ0]});Q2=makeQuery(id+"F0.imprint","IMPRINT",FACE,{"disambiguationData":[TD([[makeQuery(id+"F0.imprint","IMPRINT",EDGE,{"disambiguationData":[TD([[subQ2,1.0]])],"derivedFrom":subQ1}),1.0]])]});}
            var Q3;
            {var subQ1=sQuery(id+"F0.wireOp",EDGE,"E30");var subQ5=sQuery(id+"F0.wireOp",EDGE,"E4");var subQ6=makeQuery(id+"F0.imprint","INTERSECT",VERTEX,{"derivedFrom":[subQ5,subQ1]});Q3=makeQuery(id+"F0.imprint","IMPRINT",FACE,{"disambiguationData":[TD([[makeQuery(id+"F0.imprint","IMPRINT",EDGE,{"disambiguationData":[TD([[subQ6,1.0]])],"derivedFrom":subQ1}),-1.0]])]});}
            var Q4;
            {var subQ1=sQuery(id+"F0.wireOp",EDGE,"E29");var subQ5=sQuery(id+"F0.wireOp",EDGE,"E4");var subQ6=makeQuery(id+"F0.imprint","INTERSECT",VERTEX,{"derivedFrom":[subQ5,subQ1]});Q4=makeQuery(id+"F0.imprint","IMPRINT",FACE,{"disambiguationData":[TD([[makeQuery(id+"F0.imprint","IMPRINT",EDGE,{"disambiguationData":[TD([[subQ6,-1.0]])],"derivedFrom":subQ1}),-1.0]])]});}
            var Q5;
            {var subQ1=sQuery(id+"F0.wireOp",EDGE,"E28");var subQ5=sQuery(id+"F0.wireOp",EDGE,"E3");var subQ6=makeQuery(id+"F0.imprint","INTERSECT",VERTEX,{"derivedFrom":[subQ5,subQ1]});Q5=makeQuery(id+"F0.imprint","IMPRINT",FACE,{"disambiguationData":[TD([[makeQuery(id+"F0.imprint","IMPRINT",EDGE,{"disambiguationData":[TD([[subQ6,1.0]])],"derivedFrom":subQ1}),-1.0]])]});}
            var Q6;
            {var subQ3=sQuery(id+"F0.wireOp",EDGE,"E28");var subQ5=sQuery(id+"F0.wireOp",EDGE,"E3");var subQ6=makeQuery(id+"F0.imprint","INTERSECT",VERTEX,{"derivedFrom":[subQ5,subQ3]});Q6=makeQuery(id+"F0.imprint","IMPRINT",FACE,{"disambiguationData":[TD([[makeQuery(id+"F0.imprint","IMPRINT",EDGE,{"disambiguationData":[TD([[subQ6,-1.0]])],"derivedFrom":subQ5}),1.0]])]});}
            var Q7;
            {var subQ3=sQuery(id+"F0.wireOp",EDGE,"E23");var subQ5=sQuery(id+"F0.wireOp",EDGE,"E1");var subQ6=makeQuery(id+"F0.imprint","INTERSECT",VERTEX,{"derivedFrom":[subQ5,subQ3]});Q7=makeQuery(id+"F0.imprint","IMPRINT",FACE,{"disambiguationData":[TD([[makeQuery(id+"F0.imprint","IMPRINT",EDGE,{"disambiguationData":[TD([[subQ6,-1.0]])],"derivedFrom":subQ5}),1.0]])]});}
            var Q8;
            {var subQ1=sQuery(id+"F0.wireOp",EDGE,"E24");var subQ5=sQuery(id+"F0.wireOp",EDGE,"E2");var subQ6=makeQuery(id+"F0.imprint","INTERSECT",VERTEX,{"derivedFrom":[subQ5,subQ1]});Q8=makeQuery(id+"F0.imprint","IMPRINT",FACE,{"disambiguationData":[TD([[makeQuery(id+"F0.imprint","IMPRINT",EDGE,{"disambiguationData":[TD([[subQ6,-1.0]])],"derivedFrom":subQ1}),-1.0]])]});}
            var Q9;
            {var subQ1=sQuery(id+"F0.wireOp",EDGE,"E26");var subQ5=sQuery(id+"F0.wireOp",EDGE,"E2");var subQ6=makeQuery(id+"F0.imprint","INTERSECT",VERTEX,{"derivedFrom":[subQ5,subQ1]});Q9=makeQuery(id+"F0.imprint","IMPRINT",FACE,{"disambiguationData":[TD([[makeQuery(id+"F0.imprint","IMPRINT",EDGE,{"disambiguationData":[TD([[subQ6,-1.0]])],"derivedFrom":subQ1}),1.0]])]});}
            var Q10;
            {var subQ3=sQuery(id+"F0.wireOp",EDGE,"E26");var subQ5=sQuery(id+"F0.wireOp",EDGE,"E2");var subQ6=makeQuery(id+"F0.imprint","INTERSECT",VERTEX,{"derivedFrom":[subQ5,subQ3]});Q10=makeQuery(id+"F0.imprint","IMPRINT",FACE,{"disambiguationData":[TD([[makeQuery(id+"F0.imprint","IMPRINT",EDGE,{"disambiguationData":[TD([[subQ6,-1.0]])],"derivedFrom":subQ5}),1.0]])]});}
            var Q11;
            {var subQ1=sQuery(id+"F0.wireOp",EDGE,"E27");var subQ5=sQuery(id+"F0.wireOp",EDGE,"E3");var subQ6=makeQuery(id+"F0.imprint","INTERSECT",VERTEX,{"derivedFrom":[subQ5,subQ1]});Q11=makeQuery(id+"F0.imprint","IMPRINT",FACE,{"disambiguationData":[TD([[makeQuery(id+"F0.imprint","IMPRINT",EDGE,{"disambiguationData":[TD([[subQ6,-1.0]])],"derivedFrom":subQ1}),-1.0]])]});}
            extrude(context, id + "F8", {"entities" : qUnion([Q0, Q1, Q2, Q3, Q4, Q5, Q6, Q7, Q8, Q9, Q10, Q11]), "operationType" : NewBodyOperationType.ADD, "depth" : 3.5 * mm});
        }
        {
            var Q0;
            Q0=makeQuery(id+"F8.opExtrude","SWEPT_EDGE",EDGE,{"disambiguationData":[OSD([sQuery(id+"F0.wireOp",EDGE,"E1"),sQuery(id+"F0.wireOp",EDGE,"E2"),sQuery(id+"F0.wireOp",EDGE,"E18"),sQuery(id+"F0.wireOp",EDGE,"E19")])]});
            var Q1;
            Q1=makeQuery(id+"F8.opExtrude","SWEPT_EDGE",EDGE,{"disambiguationData":[OSD([sQuery(id+"F0.wireOp",EDGE,"E22.2"),sQuery(id+"F0.wireOp",EDGE,"E22.3"),sQuery(id+"F0.wireOp",EDGE,"E23"),sQuery(id+"F0.wireOp",EDGE,"E24")])]});
            var Q2;
            Q2=makeQuery(id+"F8.opExtrude","SWEPT_EDGE",EDGE,{"disambiguationData":[OSD([sQuery(id+"F0.wireOp",EDGE,"E2"),sQuery(id+"F0.wireOp",EDGE,"E3"),sQuery(id+"F0.wireOp",EDGE,"E16"),sQuery(id+"F0.wireOp",EDGE,"E17")])]});
            var Q3;
            Q3=makeQuery(id+"F8.opExtrude","SWEPT_EDGE",EDGE,{"disambiguationData":[OSD([sQuery(id+"F0.wireOp",EDGE,"E22.0"),sQuery(id+"F0.wireOp",EDGE,"E22.3"),sQuery(id+"F0.wireOp",EDGE,"E30"),sQuery(id+"F0.wireOp",EDGE,"E31")])]});
            var Q4;
            Q4=makeQuery(id+"F8.opExtrude","SWEPT_EDGE",EDGE,{"disambiguationData":[OSD([sQuery(id+"F0.wireOp",EDGE,"E3"),sQuery(id+"F0.wireOp",EDGE,"E4"),sQuery(id+"F0.wireOp",EDGE,"E14"),sQuery(id+"F0.wireOp",EDGE,"E15")])]});
            var Q5;
            Q5=makeQuery(id+"F8.opExtrude","SWEPT_EDGE",EDGE,{"disambiguationData":[OSD([sQuery(id+"F0.wireOp",EDGE,"E22.1"),sQuery(id+"F0.wireOp",EDGE,"E22.2"),sQuery(id+"F0.wireOp",EDGE,"E26"),sQuery(id+"F0.wireOp",EDGE,"E27")])]});
            var Q6;
            Q6=makeQuery(id+"F8.opExtrude","SWEPT_EDGE",EDGE,{"disambiguationData":[OSD([sQuery(id+"F0.wireOp",EDGE,"E22.0"),sQuery(id+"F0.wireOp",EDGE,"E22.1"),sQuery(id+"F0.wireOp",EDGE,"E28"),sQuery(id+"F0.wireOp",EDGE,"E29")])]});
            var Q7;
            Q7=makeQuery(id+"F8.opExtrude","SWEPT_EDGE",EDGE,{"disambiguationData":[OSD([sQuery(id+"F0.wireOp",EDGE,"E1"),sQuery(id+"F0.wireOp",EDGE,"E4"),sQuery(id+"F0.wireOp",EDGE,"E20"),sQuery(id+"F0.wireOp",EDGE,"E21")])]});
            fillet(context, id + "F9", {"entities" : qUnion([Q0, Q1, Q2, Q3, Q4, Q5, Q6, Q7]), "radius" : 10 * mm, "tangentPropagation" : true, "allowEdgeOverflow" : false});
        }
        {
            var Q0;
            {var subQ1=sQuery(id+"F0.wireOp",EDGE,"E48");var subQ5=sQuery(id+"F0.wireOp",EDGE,"E64");var subQ6=makeQuery(id+"F0.imprint","INTERSECT",VERTEX,{"derivedFrom":[subQ1,subQ5]});Q0=makeQuery(id+"F0.imprint","IMPRINT",FACE,{"disambiguationData":[TD([[makeQuery(id+"F0.imprint","IMPRINT",EDGE,{"disambiguationData":[TD([[subQ6,-1.0]])],"derivedFrom":subQ1}),-1.0]])]});}
            var Q1;
            {var subQ0=sQuery(id+"F0.wireOp",EDGE,"E56.rect.right");var subQ3=sQuery(id+"F0.wireOp",EDGE,"E48");var subQ4=makeQuery(id+"F0.imprint","INTERSECT",VERTEX,{"derivedFrom":[subQ3,subQ0]});Q1=makeQuery(id+"F0.imprint","IMPRINT",FACE,{"disambiguationData":[TD([[makeQuery(id+"F0.imprint","IMPRINT",EDGE,{"disambiguationData":[TD([[subQ4,-1.0]])],"derivedFrom":subQ3}),-1.0]])]});}
            var Q2;
            {var subQ0=sQuery(id+"F0.wireOp",EDGE,"E56.rect.top");var subQ3=sQuery(id+"F0.wireOp",EDGE,"E48");var subQ4=makeQuery(id+"F0.imprint","INTERSECT",VERTEX,{"derivedFrom":[subQ3,subQ0]});Q2=makeQuery(id+"F0.imprint","IMPRINT",FACE,{"disambiguationData":[TD([[makeQuery(id+"F0.imprint","IMPRINT",EDGE,{"disambiguationData":[TD([[subQ4,1.0]])],"derivedFrom":subQ3}),-1.0]])]});}
            var Q3;
            {var subQ3=sQuery(id+"F0.wireOp",EDGE,"E47");var subQ5=sQuery(id+"F0.wireOp",EDGE,"E55.rect.bottom");var subQ7=makeQuery(id+"F0.imprint","INTERSECT",VERTEX,{"derivedFrom":[subQ3,subQ5]});Q3=makeQuery(id+"F0.imprint","IMPRINT",FACE,{"disambiguationData":[TD([[makeQuery(id+"F0.imprint","IMPRINT",EDGE,{"disambiguationData":[TD([[subQ7,1.0]])],"derivedFrom":subQ3}),-1.0]])]});}
            var Q4;
            {var subQ0=sQuery(id+"F0.wireOp",EDGE,"E59.3");var subQ3=sQuery(id+"F0.wireOp",EDGE,"E45");var subQ7=makeQuery(id+"F0.imprint","INTERSECT",VERTEX,{"disambiguationData":[OD(0.0)],"derivedFrom":[subQ3,subQ0]});Q4=makeQuery(id+"F0.imprint","IMPRINT",FACE,{"disambiguationData":[TD([[makeQuery(id+"F0.imprint","IMPRINT",EDGE,{"disambiguationData":[TD([[subQ7,-1.0]])],"derivedFrom":subQ3}),-1.0]])]});}
            var Q5;
            {var subQ0=sQuery(id+"F0.wireOp",EDGE,"E59.3");var subQ3=sQuery(id+"F0.wireOp",EDGE,"E45");var subQ7=makeQuery(id+"F0.imprint","INTERSECT",VERTEX,{"disambiguationData":[OD(0.0)],"derivedFrom":[subQ3,subQ0]});Q5=makeQuery(id+"F0.imprint","IMPRINT",FACE,{"disambiguationData":[TD([[makeQuery(id+"F0.imprint","IMPRINT",EDGE,{"disambiguationData":[TD([[subQ7,1.0]])],"derivedFrom":subQ3}),-1.0]])]});}
            var Q6;
            {var subQ3=sQuery(id+"F0.wireOp",EDGE,"E47");var subQ5=sQuery(id+"F0.wireOp",EDGE,"E55.rect.right");var subQ7=makeQuery(id+"F0.imprint","INTERSECT",VERTEX,{"derivedFrom":[subQ3,subQ5]});Q6=makeQuery(id+"F0.imprint","IMPRINT",FACE,{"disambiguationData":[TD([[makeQuery(id+"F0.imprint","IMPRINT",EDGE,{"disambiguationData":[TD([[subQ7,-1.0]])],"derivedFrom":subQ3}),-1.0]])]});}
            var Q7;
            {var subQ3=sQuery(id+"F0.wireOp",EDGE,"E52");var subQ5=sQuery(id+"F0.wireOp",EDGE,"E55.rect.right");var subQ7=makeQuery(id+"F0.imprint","INTERSECT",VERTEX,{"derivedFrom":[subQ3,subQ5]});Q7=makeQuery(id+"F0.imprint","IMPRINT",FACE,{"disambiguationData":[TD([[makeQuery(id+"F0.imprint","IMPRINT",EDGE,{"disambiguationData":[TD([[subQ7,-1.0]])],"derivedFrom":subQ3}),-1.0]])]});}
            var Q8;
            {var subQ0=sQuery(id+"F0.wireOp",EDGE,"E59.2");var subQ3=sQuery(id+"F0.wireOp",EDGE,"E44");var subQ15=makeQuery(id+"F0.imprint","INTERSECT",VERTEX,{"disambiguationData":[OD(0.0)],"derivedFrom":[subQ3,subQ0]});Q8=makeQuery(id+"F0.imprint","IMPRINT",FACE,{"disambiguationData":[TD([[makeQuery(id+"F0.imprint","IMPRINT",EDGE,{"disambiguationData":[TD([[subQ15,-1.0]])],"derivedFrom":subQ3}),-1.0]])]});}
            var Q9;
            {var subQ0=sQuery(id+"F0.wireOp",EDGE,"E59.2");var subQ3=sQuery(id+"F0.wireOp",EDGE,"E44");var subQ7=makeQuery(id+"F0.imprint","INTERSECT",VERTEX,{"disambiguationData":[OD(0.0)],"derivedFrom":[subQ3,subQ0]});Q9=makeQuery(id+"F0.imprint","IMPRINT",FACE,{"disambiguationData":[TD([[makeQuery(id+"F0.imprint","IMPRINT",EDGE,{"disambiguationData":[TD([[subQ7,1.0]])],"derivedFrom":subQ3}),-1.0]])]});}
            var Q10;
            {var subQ0=sQuery(id+"F0.wireOp",EDGE,"E56.rect.top");var subQ3=sQuery(id+"F0.wireOp",EDGE,"E53");var subQ4=makeQuery(id+"F0.imprint","INTERSECT",VERTEX,{"derivedFrom":[subQ3,subQ0]});Q10=makeQuery(id+"F0.imprint","IMPRINT",FACE,{"disambiguationData":[TD([[makeQuery(id+"F0.imprint","IMPRINT",EDGE,{"disambiguationData":[TD([[subQ4,1.0]])],"derivedFrom":subQ3}),-1.0]])]});}
            var Q11;
            {var subQ0=sQuery(id+"F0.wireOp",EDGE,"E56.rect.top");var subQ3=sQuery(id+"F0.wireOp",EDGE,"E49");var subQ4=makeQuery(id+"F0.imprint","INTERSECT",VERTEX,{"derivedFrom":[subQ3,subQ0]});Q11=makeQuery(id+"F0.imprint","IMPRINT",FACE,{"disambiguationData":[TD([[makeQuery(id+"F0.imprint","IMPRINT",EDGE,{"disambiguationData":[TD([[subQ4,-1.0]])],"derivedFrom":subQ3}),-1.0]])]});}
            var Q12;
            {var subQ1=sQuery(id+"F0.wireOp",EDGE,"E49");var subQ5=sQuery(id+"F0.wireOp",EDGE,"E59.1");var subQ6=makeQuery(id+"F0.imprint","INTERSECT",VERTEX,{"disambiguationData":[OD(0.0)],"derivedFrom":[subQ1,subQ5]});Q12=makeQuery(id+"F0.imprint","IMPRINT",FACE,{"disambiguationData":[TD([[makeQuery(id+"F0.imprint","IMPRINT",EDGE,{"disambiguationData":[TD([[subQ6,1.0]])],"derivedFrom":subQ1}),-1.0]])]});}
            var Q13;
            {var subQ0=sQuery(id+"F0.wireOp",EDGE,"E59.1");var subQ3=sQuery(id+"F0.wireOp",EDGE,"E43");var subQ13=makeQuery(id+"F0.imprint","INTERSECT",VERTEX,{"disambiguationData":[OD(0.0)],"derivedFrom":[subQ3,subQ0]});Q13=makeQuery(id+"F0.imprint","IMPRINT",FACE,{"disambiguationData":[TD([[makeQuery(id+"F0.imprint","IMPRINT",EDGE,{"disambiguationData":[TD([[subQ13,-1.0]])],"derivedFrom":subQ3}),-1.0]])]});}
            var Q14;
            {var subQ0=sQuery(id+"F0.wireOp",EDGE,"E59.1");var subQ3=sQuery(id+"F0.wireOp",EDGE,"E43");var subQ4=makeQuery(id+"F0.imprint","INTERSECT",VERTEX,{"disambiguationData":[OD(0.0)],"derivedFrom":[subQ3,subQ0]});Q14=makeQuery(id+"F0.imprint","IMPRINT",FACE,{"disambiguationData":[TD([[makeQuery(id+"F0.imprint","IMPRINT",EDGE,{"disambiguationData":[TD([[subQ4,1.0]])],"derivedFrom":subQ3}),-1.0]])]});}
            var Q15;
            {var subQ3=sQuery(id+"F0.wireOp",EDGE,"E49");var subQ5=sQuery(id+"F0.wireOp",EDGE,"E55.rect.left");var subQ7=makeQuery(id+"F0.imprint","INTERSECT",VERTEX,{"derivedFrom":[subQ3,subQ5]});Q15=makeQuery(id+"F0.imprint","IMPRINT",FACE,{"disambiguationData":[TD([[makeQuery(id+"F0.imprint","IMPRINT",EDGE,{"disambiguationData":[TD([[subQ7,-1.0]])],"derivedFrom":subQ3}),-1.0]])]});}
            var Q16;
            {var subQ0=sQuery(id+"F0.wireOp",EDGE,"E56.rect.left");var subQ3=sQuery(id+"F0.wireOp",EDGE,"E50");var subQ4=makeQuery(id+"F0.imprint","INTERSECT",VERTEX,{"derivedFrom":[subQ3,subQ0]});Q16=makeQuery(id+"F0.imprint","IMPRINT",FACE,{"disambiguationData":[TD([[makeQuery(id+"F0.imprint","IMPRINT",EDGE,{"disambiguationData":[TD([[subQ4,-1.0]])],"derivedFrom":subQ3}),-1.0]])]});}
            var Q17;
            {var subQ0=sQuery(id+"F0.wireOp",EDGE,"E56.rect.left");var subQ3=sQuery(id+"F0.wireOp",EDGE,"E46");var subQ4=makeQuery(id+"F0.imprint","INTERSECT",VERTEX,{"derivedFrom":[subQ3,subQ0]});Q17=makeQuery(id+"F0.imprint","IMPRINT",FACE,{"disambiguationData":[TD([[makeQuery(id+"F0.imprint","IMPRINT",EDGE,{"disambiguationData":[TD([[subQ4,-1.0]])],"derivedFrom":subQ3}),-1.0]])]});}
            var Q18;
            {var subQ3=sQuery(id+"F0.wireOp",EDGE,"E46");var subQ5=sQuery(id+"F0.wireOp",EDGE,"E55.rect.bottom");var subQ7=makeQuery(id+"F0.imprint","INTERSECT",VERTEX,{"derivedFrom":[subQ3,subQ5]});Q18=makeQuery(id+"F0.imprint","IMPRINT",FACE,{"disambiguationData":[TD([[makeQuery(id+"F0.imprint","IMPRINT",EDGE,{"disambiguationData":[TD([[subQ7,-1.0]])],"derivedFrom":subQ3}),-1.0]])]});}
            var Q19;
            {var subQ0=sQuery(id+"F0.wireOp",EDGE,"E59.0");var subQ3=sQuery(id+"F0.wireOp",EDGE,"E42");var subQ7=makeQuery(id+"F0.imprint","INTERSECT",VERTEX,{"disambiguationData":[OD(0.0)],"derivedFrom":[subQ3,subQ0]});Q19=makeQuery(id+"F0.imprint","IMPRINT",FACE,{"disambiguationData":[TD([[makeQuery(id+"F0.imprint","IMPRINT",EDGE,{"disambiguationData":[TD([[subQ7,-1.0]])],"derivedFrom":subQ3}),-1.0]])]});}
            var Q20;
            {var subQ0=sQuery(id+"F0.wireOp",EDGE,"E59.0");var subQ3=sQuery(id+"F0.wireOp",EDGE,"E42");var subQ7=makeQuery(id+"F0.imprint","INTERSECT",VERTEX,{"disambiguationData":[OD(0.0)],"derivedFrom":[subQ3,subQ0]});Q20=makeQuery(id+"F0.imprint","IMPRINT",FACE,{"disambiguationData":[TD([[makeQuery(id+"F0.imprint","IMPRINT",EDGE,{"disambiguationData":[TD([[subQ7,1.0]])],"derivedFrom":subQ3}),-1.0]])]});}
            var Q21;
            {var subQ3=sQuery(id+"F0.wireOp",EDGE,"E50");var subQ5=sQuery(id+"F0.wireOp",EDGE,"E55.rect.bottom");var subQ7=makeQuery(id+"F0.imprint","INTERSECT",VERTEX,{"derivedFrom":[subQ3,subQ5]});Q21=makeQuery(id+"F0.imprint","IMPRINT",FACE,{"disambiguationData":[TD([[makeQuery(id+"F0.imprint","IMPRINT",EDGE,{"disambiguationData":[TD([[subQ7,-1.0]])],"derivedFrom":subQ3}),-1.0]])]});}
            var Q22;
            {var subQ1=sQuery(id+"F0.wireOp",EDGE,"E49");var subQ5=sQuery(id+"F0.wireOp",EDGE,"E66");var subQ6=makeQuery(id+"F0.imprint","INTERSECT",VERTEX,{"derivedFrom":[subQ1,subQ5]});Q22=makeQuery(id+"F0.imprint","IMPRINT",FACE,{"disambiguationData":[TD([[makeQuery(id+"F0.imprint","IMPRINT",EDGE,{"disambiguationData":[TD([[subQ6,-1.0]])],"derivedFrom":subQ1}),-1.0]])]});}
            var Q23;
            {var subQ0=sQuery(id+"F0.wireOp",EDGE,"E62");var subQ1=sQuery(id+"F0.wireOp",EDGE,"E46");var subQ2=makeQuery(id+"F0.imprint","INTERSECT",VERTEX,{"derivedFrom":[subQ1,subQ0]});Q23=makeQuery(id+"F0.imprint","IMPRINT",FACE,{"disambiguationData":[TD([[makeQuery(id+"F0.imprint","IMPRINT",EDGE,{"disambiguationData":[TD([[subQ2,1.0]])],"derivedFrom":subQ1}),-1.0]])]});}
            var Q24;
            {var subQ0=sQuery(id+"F0.wireOp",EDGE,"E63");var subQ1=sQuery(id+"F0.wireOp",EDGE,"E46");var subQ2=makeQuery(id+"F0.imprint","INTERSECT",VERTEX,{"derivedFrom":[subQ1,subQ0]});Q24=makeQuery(id+"F0.imprint","IMPRINT",FACE,{"disambiguationData":[TD([[makeQuery(id+"F0.imprint","IMPRINT",EDGE,{"disambiguationData":[TD([[subQ2,1.0]])],"derivedFrom":subQ1}),-1.0]])]});}
            var Q25;
            {var subQ0=sQuery(id+"F0.wireOp",EDGE,"E61");var subQ1=sQuery(id+"F0.wireOp",EDGE,"E47");var subQ2=makeQuery(id+"F0.imprint","INTERSECT",VERTEX,{"derivedFrom":[subQ1,subQ0]});Q25=makeQuery(id+"F0.imprint","IMPRINT",FACE,{"disambiguationData":[TD([[makeQuery(id+"F0.imprint","IMPRINT",EDGE,{"disambiguationData":[TD([[subQ2,-1.0]])],"derivedFrom":subQ1}),-1.0]])]});}
            var Q26;
            {var subQ0=sQuery(id+"F0.wireOp",EDGE,"E60");var subQ1=sQuery(id+"F0.wireOp",EDGE,"E47");var subQ2=makeQuery(id+"F0.imprint","INTERSECT",VERTEX,{"derivedFrom":[subQ1,subQ0]});Q26=makeQuery(id+"F0.imprint","IMPRINT",FACE,{"disambiguationData":[TD([[makeQuery(id+"F0.imprint","IMPRINT",EDGE,{"disambiguationData":[TD([[subQ2,-1.0]])],"derivedFrom":subQ1}),-1.0]])]});}
            var Q27;
            {var subQ1=sQuery(id+"F0.wireOp",EDGE,"E48");var subQ5=sQuery(id+"F0.wireOp",EDGE,"E59.2");var subQ6=makeQuery(id+"F0.imprint","INTERSECT",VERTEX,{"disambiguationData":[OD(0.0)],"derivedFrom":[subQ1,subQ5]});Q27=makeQuery(id+"F0.imprint","IMPRINT",FACE,{"disambiguationData":[TD([[makeQuery(id+"F0.imprint","IMPRINT",EDGE,{"disambiguationData":[TD([[subQ6,-1.0]])],"derivedFrom":subQ1}),-1.0]])]});}
            var Q28;
            {var subQ3=sQuery(id+"F0.wireOp",EDGE,"E47");var subQ5=sQuery(id+"F0.wireOp",EDGE,"E59.3");var subQ6=makeQuery(id+"F0.imprint","INTERSECT",VERTEX,{"disambiguationData":[OD(1.0)],"derivedFrom":[subQ3,subQ5]});Q28=makeQuery(id+"F0.imprint","IMPRINT",FACE,{"disambiguationData":[TD([[makeQuery(id+"F0.imprint","IMPRINT",EDGE,{"disambiguationData":[TD([[subQ6,-1.0]])],"derivedFrom":subQ3}),-1.0]])]});}
            var Q29;
            {var subQ0=sQuery(id+"F0.wireOp",EDGE,"E59.3");var subQ1=sQuery(id+"F0.wireOp",EDGE,"E47");var subQ2=makeQuery(id+"F0.imprint","INTERSECT",VERTEX,{"disambiguationData":[OD(0.0)],"derivedFrom":[subQ1,subQ0]});Q29=makeQuery(id+"F0.imprint","IMPRINT",FACE,{"disambiguationData":[TD([[makeQuery(id+"F0.imprint","IMPRINT",EDGE,{"disambiguationData":[TD([[subQ2,-1.0]])],"derivedFrom":subQ1}),-1.0]])]});}
            var Q30;
            {var subQ0=sQuery(id+"F0.wireOp",EDGE,"E59.3");var subQ1=sQuery(id+"F0.wireOp",EDGE,"E47");var subQ2=makeQuery(id+"F0.imprint","INTERSECT",VERTEX,{"disambiguationData":[OD(0.0)],"derivedFrom":[subQ1,subQ0]});Q30=makeQuery(id+"F0.imprint","IMPRINT",FACE,{"disambiguationData":[TD([[makeQuery(id+"F0.imprint","IMPRINT",EDGE,{"disambiguationData":[TD([[subQ2,1.0]])],"derivedFrom":subQ1}),-1.0]])]});}
            var Q31;
            {var subQ0=sQuery(id+"F0.wireOp",EDGE,"E62");var subQ1=sQuery(id+"F0.wireOp",EDGE,"E46");var subQ2=makeQuery(id+"F0.imprint","INTERSECT",VERTEX,{"derivedFrom":[subQ1,subQ0]});Q31=makeQuery(id+"F0.imprint","IMPRINT",FACE,{"disambiguationData":[TD([[makeQuery(id+"F0.imprint","IMPRINT",EDGE,{"disambiguationData":[TD([[subQ2,-1.0]])],"derivedFrom":subQ1}),-1.0]])]});}
            var Q32;
            {var subQ0=sQuery(id+"F0.wireOp",EDGE,"E59.0");var subQ1=sQuery(id+"F0.wireOp",EDGE,"E46");var subQ2=makeQuery(id+"F0.imprint","INTERSECT",VERTEX,{"disambiguationData":[OD(0.0)],"derivedFrom":[subQ1,subQ0]});Q32=makeQuery(id+"F0.imprint","IMPRINT",FACE,{"disambiguationData":[TD([[makeQuery(id+"F0.imprint","IMPRINT",EDGE,{"disambiguationData":[TD([[subQ2,-1.0]])],"derivedFrom":subQ1}),-1.0]])]});}
            var Q33;
            {var subQ1=sQuery(id+"F0.wireOp",EDGE,"E46");var subQ5=sQuery(id+"F0.wireOp",EDGE,"E55.rect.left");var subQ7=makeQuery(id+"F0.imprint","INTERSECT",VERTEX,{"derivedFrom":[subQ1,subQ5]});Q33=makeQuery(id+"F0.imprint","IMPRINT",FACE,{"disambiguationData":[TD([[makeQuery(id+"F0.imprint","IMPRINT",EDGE,{"disambiguationData":[TD([[subQ7,-1.0]])],"derivedFrom":subQ1}),-1.0]])]});}
            var Q34;
            {var subQ1=sQuery(id+"F0.wireOp",EDGE,"E49");var subQ5=sQuery(id+"F0.wireOp",EDGE,"E55.rect.left");var subQ7=makeQuery(id+"F0.imprint","INTERSECT",VERTEX,{"derivedFrom":[subQ1,subQ5]});Q34=makeQuery(id+"F0.imprint","IMPRINT",FACE,{"disambiguationData":[TD([[makeQuery(id+"F0.imprint","IMPRINT",EDGE,{"disambiguationData":[TD([[subQ7,1.0]])],"derivedFrom":subQ1}),-1.0]])]});}
            var Q35;
            {var subQ1=sQuery(id+"F0.wireOp",EDGE,"E49");var subQ5=sQuery(id+"F0.wireOp",EDGE,"E59.1");var subQ6=makeQuery(id+"F0.imprint","INTERSECT",VERTEX,{"disambiguationData":[OD(1.0)],"derivedFrom":[subQ1,subQ5]});Q35=makeQuery(id+"F0.imprint","IMPRINT",FACE,{"disambiguationData":[TD([[makeQuery(id+"F0.imprint","IMPRINT",EDGE,{"disambiguationData":[TD([[subQ6,-1.0]])],"derivedFrom":subQ1}),-1.0]])]});}
            var Q36;
            {var subQ1=sQuery(id+"F0.wireOp",EDGE,"E49");var subQ5=sQuery(id+"F0.wireOp",EDGE,"E55.rect.top");var subQ7=makeQuery(id+"F0.imprint","INTERSECT",VERTEX,{"derivedFrom":[subQ1,subQ5]});Q36=makeQuery(id+"F0.imprint","IMPRINT",FACE,{"disambiguationData":[TD([[makeQuery(id+"F0.imprint","IMPRINT",EDGE,{"disambiguationData":[TD([[subQ7,-1.0]])],"derivedFrom":subQ1}),-1.0]])]});}
            var Q37;
            {var subQ0=sQuery(id+"F0.wireOp",EDGE,"E65");var subQ1=sQuery(id+"F0.wireOp",EDGE,"E48");var subQ2=makeQuery(id+"F0.imprint","INTERSECT",VERTEX,{"derivedFrom":[subQ1,subQ0]});Q37=makeQuery(id+"F0.imprint","IMPRINT",FACE,{"disambiguationData":[TD([[makeQuery(id+"F0.imprint","IMPRINT",EDGE,{"disambiguationData":[TD([[subQ2,-1.0]])],"derivedFrom":subQ1}),-1.0]])]});}
            var Q38;
            {var subQ0=sQuery(id+"F0.wireOp",EDGE,"E59.2");var subQ1=sQuery(id+"F0.wireOp",EDGE,"E48");var subQ2=makeQuery(id+"F0.imprint","INTERSECT",VERTEX,{"disambiguationData":[OD(1.0)],"derivedFrom":[subQ1,subQ0]});Q38=makeQuery(id+"F0.imprint","IMPRINT",FACE,{"disambiguationData":[TD([[makeQuery(id+"F0.imprint","IMPRINT",EDGE,{"disambiguationData":[TD([[subQ2,-1.0]])],"derivedFrom":subQ1}),-1.0]])]});}
            var Q39;
            {var subQ1=sQuery(id+"F0.wireOp",EDGE,"E48");var subQ5=sQuery(id+"F0.wireOp",EDGE,"E55.rect.right");var subQ7=makeQuery(id+"F0.imprint","INTERSECT",VERTEX,{"derivedFrom":[subQ1,subQ5]});Q39=makeQuery(id+"F0.imprint","IMPRINT",FACE,{"disambiguationData":[TD([[makeQuery(id+"F0.imprint","IMPRINT",EDGE,{"disambiguationData":[TD([[subQ7,-1.0]])],"derivedFrom":subQ1}),-1.0]])]});}
            extrude(context, id + "F10", {"entities" : qUnion([Q0, Q1, Q2, Q3, Q4, Q5, Q6, Q7, Q8, Q9, Q10, Q11, Q12, Q13, Q14, Q15, Q16, Q17, Q18, Q19, Q20, Q21, Q22, Q23, Q24, Q25, Q26, Q27, Q28, Q29, Q30, Q31, Q32, Q33, Q34, Q35, Q36, Q37, Q38, Q39]), "depth" : 2 * mm});
        }
        {
            var Q0;
            Q0=makeQuery(id+"F10.opExtrude","SWEPT_EDGE",EDGE,{"disambiguationData":[OSD([sQuery(id+"F0.wireOp",EDGE,"E52"),sQuery(id+"F0.wireOp",EDGE,"E55.rect.bottom")])]});
            var Q1;
            Q1=makeQuery(id+"F10.opExtrude","SWEPT_EDGE",EDGE,{"disambiguationData":[OSD([sQuery(id+"F0.wireOp",EDGE,"E53"),sQuery(id+"F0.wireOp",EDGE,"E56.rect.top")])]});
            var Q2;
            Q2=makeQuery(id+"F10.opExtrude","SWEPT_EDGE",EDGE,{"disambiguationData":[OSD([sQuery(id+"F0.wireOp",EDGE,"E46"),sQuery(id+"F0.wireOp",EDGE,"E55.rect.bottom")])]});
            var Q3;
            Q3=makeQuery(id+"F10.opExtrude","SWEPT_EDGE",EDGE,{"disambiguationData":[OSD([sQuery(id+"F0.wireOp",EDGE,"E49"),sQuery(id+"F0.wireOp",EDGE,"E56.rect.top")])]});
            var Q4;
            Q4=makeQuery(id+"F10.opExtrude","SWEPT_EDGE",EDGE,{"disambiguationData":[OSD([sQuery(id+"F0.wireOp",EDGE,"E50"),sQuery(id+"F0.wireOp",EDGE,"E55.rect.bottom")])]});
            var Q5;
            Q5=makeQuery(id+"F10.opExtrude","SWEPT_EDGE",EDGE,{"disambiguationData":[OSD([sQuery(id+"F0.wireOp",EDGE,"E47"),sQuery(id+"F0.wireOp",EDGE,"E55.rect.bottom")])]});
            var Q6;
            Q6=makeQuery(id+"F10.opExtrude","SWEPT_EDGE",EDGE,{"disambiguationData":[OSD([sQuery(id+"F0.wireOp",EDGE,"E48"),sQuery(id+"F0.wireOp",EDGE,"E56.rect.top")])]});
            var Q7;
            Q7=makeQuery(id+"F10.opExtrude","SWEPT_EDGE",EDGE,{"disambiguationData":[OSD([sQuery(id+"F0.wireOp",EDGE,"E54"),sQuery(id+"F0.wireOp",EDGE,"E56.rect.top")])]});
            var Q8;
            Q8=makeQuery(id+"F10.opExtrude","SWEPT_EDGE",EDGE,{"disambiguationData":[OSD([sQuery(id+"F0.wireOp",EDGE,"E55.rect.top"),sQuery(id+"F0.wireOp",EDGE,"E55.rect.right"),sQuery(id+"F0.wireOp",EDGE,"E64")])]});
            var Q9;
            Q9=makeQuery(id+"F10.opExtrude","SWEPT_EDGE",EDGE,{"disambiguationData":[OSD([sQuery(id+"F0.wireOp",EDGE,"E55.rect.top"),sQuery(id+"F0.wireOp",EDGE,"E55.rect.left"),sQuery(id+"F0.wireOp",EDGE,"E67")])]});
            var Q10;
            Q10=makeQuery(id+"F10.opExtrude","SWEPT_EDGE",EDGE,{"disambiguationData":[OSD([sQuery(id+"F0.wireOp",EDGE,"E55.rect.bottom"),sQuery(id+"F0.wireOp",EDGE,"E55.rect.left"),sQuery(id+"F0.wireOp",EDGE,"E63")])]});
            var Q11;
            Q11=makeQuery(id+"F10.opExtrude","SWEPT_EDGE",EDGE,{"disambiguationData":[OSD([sQuery(id+"F0.wireOp",EDGE,"E55.rect.bottom"),sQuery(id+"F0.wireOp",EDGE,"E55.rect.right"),sQuery(id+"F0.wireOp",EDGE,"E60")])]});
            var Q12;
            Q12=makeQuery(id+"F10.opExtrude","SWEPT_EDGE",EDGE,{"disambiguationData":[OSD([sQuery(id+"F0.wireOp",EDGE,"E46"),sQuery(id+"F0.wireOp",EDGE,"E55.rect.left")])]});
            var Q13;
            Q13=makeQuery(id+"F10.opExtrude","SWEPT_EDGE",EDGE,{"disambiguationData":[OSD([sQuery(id+"F0.wireOp",EDGE,"E47"),sQuery(id+"F0.wireOp",EDGE,"E55.rect.right")])]});
            var Q14;
            Q14=makeQuery(id+"F10.opExtrude","SWEPT_EDGE",EDGE,{"disambiguationData":[OSD([sQuery(id+"F0.wireOp",EDGE,"E56.rect.bottom"),sQuery(id+"F0.wireOp",EDGE,"E56.rect.right")])]});
            var Q15;
            Q15=makeQuery(id+"F10.opExtrude","SWEPT_EDGE",EDGE,{"disambiguationData":[OSD([sQuery(id+"F0.wireOp",EDGE,"E56.rect.bottom"),sQuery(id+"F0.wireOp",EDGE,"E56.rect.left")])]});
            fillet(context, id + "F11", {"entities" : qUnion([Q0, Q1, Q2, Q3, Q4, Q5, Q6, Q7, Q8, Q9, Q10, Q11, Q12, Q13, Q14, Q15]), "radius" : 1.5 * mm, "tangentPropagation" : true, "allowEdgeOverflow" : false});
        }
        {
            var Q0;
            {var subQ0=sQuery(id+"F0.wireOp",EDGE,"E38");var subQ1=sQuery(id+"F0.wireOp",EDGE,"E24");Q0=makeQuery(id+"F8.boolean.opBoolean","SPLIT",EDGE,{"disambiguationData":[topologyDisambiguationEdgeConnected([makeQuery(id+"F5.opExtrude","SWEPT_FACE",FACE,{"disambiguationData":[OSD([subQ0])]})])],"derivedFrom":makeQuery(id+"F8.opExtrude","SWEPT_EDGE",EDGE,{"disambiguationData":[OSD([subQ1,subQ0])]})});}
            var Q1;
            {var subQ0=sQuery(id+"F0.wireOp",EDGE,"E38");var subQ1=sQuery(id+"F0.wireOp",EDGE,"E26");Q1=makeQuery(id+"F8.boolean.opBoolean","SPLIT",EDGE,{"disambiguationData":[topologyDisambiguationEdgeConnected([makeQuery(id+"F5.opExtrude","SWEPT_FACE",FACE,{"disambiguationData":[OSD([subQ0])]})])],"derivedFrom":makeQuery(id+"F8.opExtrude","SWEPT_EDGE",EDGE,{"disambiguationData":[OSD([subQ1,subQ0])]})});}
            var Q2;
            {var subQ0=sQuery(id+"F0.wireOp",EDGE,"E40");var subQ1=sQuery(id+"F0.wireOp",EDGE,"E28");Q2=makeQuery(id+"F8.boolean.opBoolean","SPLIT",EDGE,{"disambiguationData":[topologyDisambiguationEdgeConnected([makeQuery(id+"F5.opExtrude","SWEPT_FACE",FACE,{"disambiguationData":[OSD([subQ0])]})])],"derivedFrom":makeQuery(id+"F8.opExtrude","SWEPT_EDGE",EDGE,{"disambiguationData":[OSD([subQ1,subQ0])]})});}
            var Q3;
            {var subQ0=sQuery(id+"F0.wireOp",EDGE,"E40");var subQ1=sQuery(id+"F0.wireOp",EDGE,"E27");Q3=makeQuery(id+"F8.boolean.opBoolean","SPLIT",EDGE,{"disambiguationData":[topologyDisambiguationEdgeConnected([makeQuery(id+"F5.opExtrude","SWEPT_FACE",FACE,{"disambiguationData":[OSD([subQ0])]})])],"derivedFrom":makeQuery(id+"F8.opExtrude","SWEPT_EDGE",EDGE,{"disambiguationData":[OSD([subQ1,subQ0])]})});}
            var Q4;
            {var subQ0=sQuery(id+"F0.wireOp",EDGE,"E33");var subQ1=sQuery(id+"F0.wireOp",EDGE,"E30");Q4=makeQuery(id+"F8.boolean.opBoolean","SPLIT",EDGE,{"disambiguationData":[topologyDisambiguationEdgeConnected([makeQuery(id+"F5.opExtrude","SWEPT_FACE",FACE,{"disambiguationData":[OSD([subQ0])]})])],"derivedFrom":makeQuery(id+"F8.opExtrude","SWEPT_EDGE",EDGE,{"disambiguationData":[OSD([subQ1,subQ0])]})});}
            var Q5;
            {var subQ0=sQuery(id+"F0.wireOp",EDGE,"E33");var subQ1=sQuery(id+"F0.wireOp",EDGE,"E29");Q5=makeQuery(id+"F8.boolean.opBoolean","SPLIT",EDGE,{"disambiguationData":[topologyDisambiguationEdgeConnected([makeQuery(id+"F5.opExtrude","SWEPT_FACE",FACE,{"disambiguationData":[OSD([subQ0])]})])],"derivedFrom":makeQuery(id+"F8.opExtrude","SWEPT_EDGE",EDGE,{"disambiguationData":[OSD([subQ1,subQ0])]})});}
            var Q6;
            {var subQ0=sQuery(id+"F0.wireOp",EDGE,"E36");var subQ1=sQuery(id+"F0.wireOp",EDGE,"E23");Q6=makeQuery(id+"F8.boolean.opBoolean","SPLIT",EDGE,{"disambiguationData":[topologyDisambiguationEdgeConnected([makeQuery(id+"F5.opExtrude","SWEPT_FACE",FACE,{"disambiguationData":[OSD([subQ0])]})])],"derivedFrom":makeQuery(id+"F8.opExtrude","SWEPT_EDGE",EDGE,{"disambiguationData":[OSD([subQ1,subQ0])]})});}
            var Q7;
            {var subQ0=sQuery(id+"F0.wireOp",EDGE,"E36");var subQ1=sQuery(id+"F0.wireOp",EDGE,"E31");Q7=makeQuery(id+"F8.boolean.opBoolean","SPLIT",EDGE,{"disambiguationData":[topologyDisambiguationEdgeConnected([makeQuery(id+"F5.opExtrude","SWEPT_FACE",FACE,{"disambiguationData":[OSD([subQ0])]})])],"derivedFrom":makeQuery(id+"F8.opExtrude","SWEPT_EDGE",EDGE,{"disambiguationData":[OSD([subQ1,subQ0])]})});}
            fillet(context, id + "F12", {"entities" : qUnion([Q0, Q1, Q2, Q3, Q4, Q5, Q6, Q7]), "radius" : 4 * mm, "tangentPropagation" : true, "allowEdgeOverflow" : false});
        }
    });
